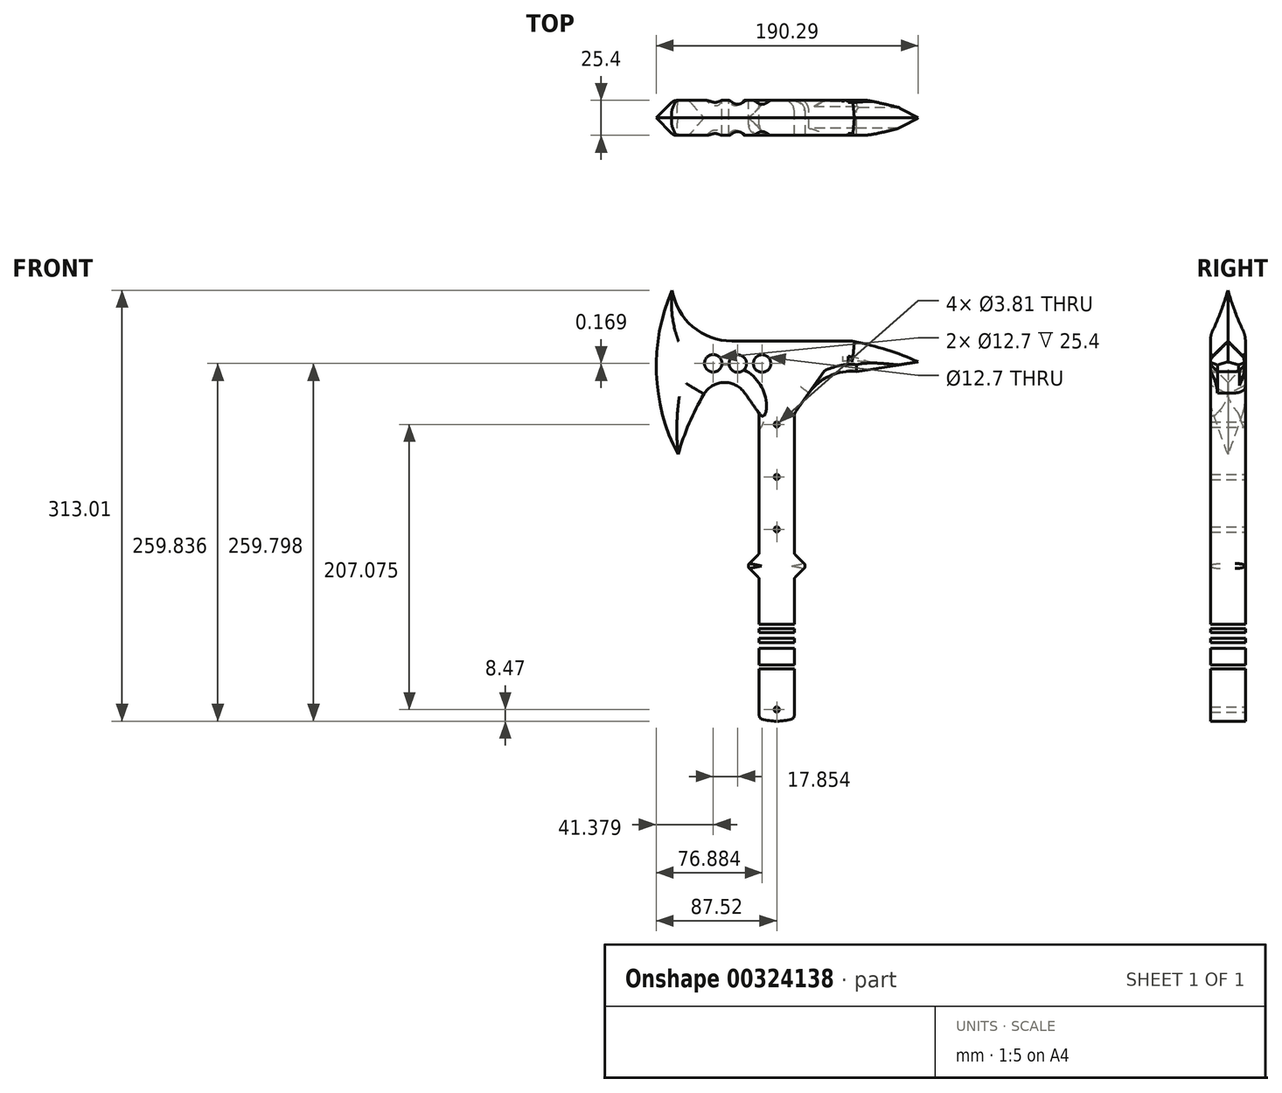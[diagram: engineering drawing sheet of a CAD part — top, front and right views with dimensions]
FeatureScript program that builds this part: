
annotation { "Feature Type Name" : "Feature", "Feature Type Description" : "" }
export const myFeature = defineFeature(function(context is Context, id is Id, definition is map)
    precondition{}
    {
        {
            var Q0;
            Q0=qCreatedBy(makeId("Front.planeOp"),FACE);
            var sketch = newSketch(context, id + "F0", { "sketchPlane" : qUnion([Q0])});
            skLineSegment(sketch, "E0", {"start": v(0, 35.02) * mm, "end": v(0, -35.92) * mm, "construction": true});
            skLineSegment(sketch, "E1", {"start": v(-43.38, 0) * mm, "end": v(43.38, 0) * mm, "construction": true});
            skLineSegment(sketch, "E2", {"start": v(-43.38, 44.66) * mm, "end": v(-43.38, -49.27) * mm, "construction": true});
            skLineSegment(sketch, "E3", {"start": v(43.38, 41.6) * mm, "end": v(43.38, -50.81) * mm, "construction": true});
            skLineSegment(sketch, "E4", {"start": v(58.14, -35.92) * mm, "end": v(-58.32, -35.92) * mm, "construction": true});
            skLineSegment(sketch, "E5", {"start": v(49.26, 35.02) * mm, "end": v(-56.77, 35.02) * mm, "construction": true});
            skArc(sketch, "E6", {"start": v(-10.89, -36.51) * mm, "mid": v(0, -38.1) * mm, "end": v(10.89, -36.51) * mm});
            skLineSegment(sketch, "E7", {"start": v(-12.7, -34.08) * mm, "end": v(-12.7, 64.63) * mm});
            skLineSegment(sketch, "E8", {"start": v(12.7, -34.08) * mm, "end": v(12.7, 64.63) * mm});
            skLineSegment(sketch, "E9", {"start": v(-13.44, 66.42) * mm, "end": v(-19.88, 72.86) * mm});
            skLineSegment(sketch, "E10", {"start": v(-19.88, 76.46) * mm, "end": v(-13.44, 82.9) * mm});
            skLineSegment(sketch, "E11", {"start": v(13.44, 66.42) * mm, "end": v(19.88, 72.86) * mm});
            skLineSegment(sketch, "E12", {"start": v(19.88, 76.46) * mm, "end": v(13.44, 82.9) * mm});
            skLineSegment(sketch, "E13", {"start": v(-12.7, 84.7) * mm, "end": v(-12.7, 183.24) * mm});
            skLineSegment(sketch, "E14", {"start": v(12.7, 84.7) * mm, "end": v(12.7, 183.24) * mm});
            skCircle(sketch, "E15", {"center": v(0, -29.63) * mm, "radius": 1.9 * mm});
            skLineSegment(sketch, "E16", {"start": v(-13.85, 186.88) * mm, "end": v(-23.3, 200.37) * mm});
            skLineSegment(sketch, "E17", {"start": v(13.85, 186.88) * mm, "end": v(23.3, 200.37) * mm});
            skArc(sketch, "E18", {"start": v(23.3, 200.37) * mm, "mid": v(0, 210.13) * mm, "end": v(-23.3, 200.37) * mm});
            skArc(sketch, "E19", {"start": v(57.98, 215.9) * mm, "mid": v(38.62, 212.64) * mm, "end": v(23.3, 200.37) * mm});
            skLineSegment(sketch, "E20", {"start": v(57.98, 215.9) * mm, "end": v(102.77, 222.96) * mm});
            skLineSegment(sketch, "E21", {"start": v(54.6, 176.96) * mm, "end": v(54.6, 259.28) * mm, "construction": true});
            skArc(sketch, "E22", {"start": v(102.77, 222.96) * mm, "mid": v(79.13, 231.9) * mm, "end": v(54.6, 238.02) * mm});
            skLineSegment(sketch, "E23", {"start": v(54.6, 238.02) * mm, "end": v(-32.59, 238.02) * mm});
            skArc(sketch, "E24", {"start": v(-75.92, 274.91) * mm, "mid": v(-61.04, 248.5) * mm, "end": v(-32.59, 238.02) * mm});
            skArc(sketch, "E25", {"start": v(-75.92, 274.91) * mm, "mid": v(-87.43, 214.8) * mm, "end": v(-71.62, 155.66) * mm});
            skArc(sketch, "E26", {"start": v(-23.3, 200.37) * mm, "mid": v(-38.34, 207.92) * mm, "end": v(-52.92, 199.5) * mm});
            skArc(sketch, "E27", {"start": v(-52.92, 199.5) * mm, "mid": v(-63.68, 178.18) * mm, "end": v(-71.62, 155.66) * mm});
            skLineSegment(sketch, "E28", {"start": v(-12.7, -25.44) * mm, "end": v(12.7, -25.44) * mm});
            skLineSegment(sketch, "E29", {"start": v(-12.7, -21.2) * mm, "end": v(12.7, -21.2) * mm});
            skLineSegment(sketch, "E30", {"start": v(-12.7, -17) * mm, "end": v(12.7, -17) * mm});
            skLineSegment(sketch, "E31", {"start": v(-12.7, -17) * mm, "end": v(-12.7, -12.4) * mm});
            skLineSegment(sketch, "E32", {"start": v(-12.7, -12.4) * mm, "end": v(12.7, -12.4) * mm});
            skLineSegment(sketch, "E33", {"start": v(12.7, -12.4) * mm, "end": v(12.7, -17) * mm});
            skLineSegment(sketch, "E34", {"start": v(-12.7, -21.2) * mm, "end": v(-12.7, -25.44) * mm});
            skLineSegment(sketch, "E35", {"start": v(12.7, -21.2) * mm, "end": v(12.7, -25.44) * mm});
            skLineSegment(sketch, "E36", {"start": v(-12.7, -8.39) * mm, "end": v(12.7, -8.39) * mm});
            skLineSegment(sketch, "E37", {"start": v(12.7, -8.39) * mm, "end": v(12.7, -4.18) * mm});
            skLineSegment(sketch, "E38", {"start": v(12.7, -4.18) * mm, "end": v(-12.7, -4.18) * mm});
            skLineSegment(sketch, "E39", {"start": v(-12.7, -4.18) * mm, "end": v(-12.7, -8.39) * mm});
            skLineSegment(sketch, "E40", {"start": v(-12.7, 0) * mm, "end": v(-12.7, 2.84) * mm});
            skLineSegment(sketch, "E41", {"start": v(-12.7, 2.84) * mm, "end": v(12.7, 2.84) * mm});
            skLineSegment(sketch, "E42", {"start": v(12.7, 2.84) * mm, "end": v(12.7, 0) * mm});
            skLineSegment(sketch, "E43", {"start": v(12.7, 0) * mm, "end": v(-12.7, 0) * mm});
            skLineSegment(sketch, "E44", {"start": v(-12.7, 14.88) * mm, "end": v(-12.7, 18.87) * mm});
            skLineSegment(sketch, "E45", {"start": v(-12.7, 18.87) * mm, "end": v(12.7, 18.87) * mm});
            skLineSegment(sketch, "E46", {"start": v(12.7, 18.87) * mm, "end": v(12.7, 14.88) * mm});
            skLineSegment(sketch, "E47", {"start": v(12.7, 14.88) * mm, "end": v(-12.7, 14.88) * mm});
            skLineSegment(sketch, "E48", {"start": v(-12.7, 22.28) * mm, "end": v(-12.7, 26.29) * mm});
            skLineSegment(sketch, "E49", {"start": v(-12.7, 26.29) * mm, "end": v(12.7, 26.29) * mm});
            skLineSegment(sketch, "E50", {"start": v(12.7, 26.29) * mm, "end": v(12.7, 22.22) * mm});
            skLineSegment(sketch, "E51", {"start": v(12.7, 22.22) * mm, "end": v(-12.7, 22.28) * mm});
            skLineSegment(sketch, "E52", {"start": v(-12.7, 29.04) * mm, "end": v(-12.7, 32.42) * mm});
            skLineSegment(sketch, "E53", {"start": v(-12.7, 32.42) * mm, "end": v(12.7, 32.42) * mm});
            skLineSegment(sketch, "E54", {"start": v(12.7, 32.42) * mm, "end": v(12.7, 29.04) * mm});
            skLineSegment(sketch, "E55", {"start": v(12.7, 29.04) * mm, "end": v(-12.7, 29.04) * mm});
            skLineSegment(sketch, "E56", {"start": v(-12.7, 35.9) * mm, "end": v(12.7, 35.9) * mm});
            skLineSegment(sketch, "E57", {"start": v(12.7, 35.9) * mm, "end": v(12.7, 39.28) * mm});
            skLineSegment(sketch, "E58", {"start": v(12.7, 39.28) * mm, "end": v(-12.7, 39.28) * mm});
            skLineSegment(sketch, "E59", {"start": v(-12.7, 39.28) * mm, "end": v(-12.7, 35.9) * mm});
            skCircle(sketch, "E60", {"center": v(0, 101.25) * mm, "radius": 1.9 * mm});
            skCircle(sketch, "E61", {"center": v(0, 139.35) * mm, "radius": 1.9 * mm});
            skCircle(sketch, "E62", {"center": v(0, 177.45) * mm, "radius": 1.9 * mm});
            skLineSegment(sketch, "E63.0", {"start": v(54.6, 221.8) * mm, "end": v(78.22, 225.52) * mm});
            skArc(sketch, "E63.1", {"start": v(78.22, 225.52) * mm, "mid": v(26.91, 235.06) * mm, "end": v(-25.16, 231.67) * mm});
            skLineSegment(sketch, "E63.2", {"start": v(-25.16, 231.67) * mm, "end": v(-32.59, 231.67) * mm});
            skArc(sketch, "E63.4", {"start": v(-58.36, 202.77) * mm, "mid": v(-66.1, 188.24) * mm, "end": v(-72.57, 173.1) * mm});
            skArc(sketch, "E63.5", {"start": v(-75.9, 256.46) * mm, "mid": v(-81.07, 214.5) * mm, "end": v(-72.57, 173.1) * mm});
            skArc(sketch, "E63.6", {"start": v(-75.9, 256.46) * mm, "mid": v(-57.54, 238.3) * mm, "end": v(-32.59, 231.67) * mm});
            skArc(sketch, "E64", {"start": v(54.6, 221.8) * mm, "mid": v(37, 213.93) * mm, "end": v(23.3, 200.37) * mm});
            skArc(sketch, "E65", {"start": v(-23.3, 200.37) * mm, "mid": v(-40.1, 212.15) * mm, "end": v(-58.36, 202.77) * mm});
            skLineSegment(sketch, "E66", {"start": v(0, 227.4) * mm, "end": v(0, 218.31) * mm});
            skLineSegment(sketch, "E67", {"start": v(-75.92, 274.91) * mm, "end": v(-75.9, 256.46) * mm});
            skLineSegment(sketch, "E68", {"start": v(-72.57, 173.1) * mm, "end": v(-71.62, 155.66) * mm});
            skLineSegment(sketch, "E69", {"start": v(78.22, 225.52) * mm, "end": v(102.77, 222.96) * mm});
            skCircle(sketch, "E70", {"center": v(-28.29, 221.7) * mm, "radius": 6.35 * mm});
            skCircle(sketch, "E71", {"center": v(-10.64, 221.74) * mm, "radius": 6.35 * mm});
            skCircle(sketch, "E72", {"center": v(-46.14, 221.87) * mm, "radius": 6.35 * mm});
            skPoint(sketch, "E73.visualSharp", {"position": v(21.68, 74.66) * mm});
            skArc(sketch, "E73.filletArc", {"start": v(19.88, 72.86) * mm, "mid": v(20.63, 74.66) * mm, "end": v(19.88, 76.46) * mm});
            skPoint(sketch, "E74.visualSharp", {"position": v(-21.68, 74.66) * mm});
            skArc(sketch, "E74.filletArc", {"start": v(-19.88, 76.46) * mm, "mid": v(-20.63, 74.66) * mm, "end": v(-19.88, 72.86) * mm});
            skPoint(sketch, "E75.visualSharp", {"position": v(-12.7, 65.68) * mm});
            skArc(sketch, "E75.filletArc", {"start": v(-12.7, 64.63) * mm, "mid": v(-12.9, 65.6) * mm, "end": v(-13.44, 66.42) * mm});
            skPoint(sketch, "E76.visualSharp", {"position": v(-12.7, 83.64) * mm});
            skArc(sketch, "E76.filletArc", {"start": v(-13.44, 82.9) * mm, "mid": v(-12.9, 83.72) * mm, "end": v(-12.7, 84.7) * mm});
            skPoint(sketch, "E77.visualSharp", {"position": v(12.7, 83.64) * mm});
            skArc(sketch, "E77.filletArc", {"start": v(12.7, 84.7) * mm, "mid": v(12.9, 83.72) * mm, "end": v(13.44, 82.9) * mm});
            skPoint(sketch, "E78.visualSharp", {"position": v(12.7, 65.68) * mm});
            skArc(sketch, "E78.filletArc", {"start": v(13.44, 66.42) * mm, "mid": v(12.9, 65.6) * mm, "end": v(12.7, 64.63) * mm});
            skPoint(sketch, "E79.visualSharp", {"position": v(-12.7, -35.92) * mm});
            skArc(sketch, "E79.filletArc", {"start": v(-12.7, -34.08) * mm, "mid": v(-12.2, -35.6) * mm, "end": v(-10.89, -36.51) * mm});
            skPoint(sketch, "E80.visualSharp", {"position": v(12.7, -35.92) * mm});
            skArc(sketch, "E80.filletArc", {"start": v(10.89, -36.51) * mm, "mid": v(12.2, -35.6) * mm, "end": v(12.7, -34.08) * mm});
            skLineSegment(sketch, "E81", {"start": v(0, -99) * mm, "end": v(0, 328.41) * mm, "construction": true});
            skPoint(sketch, "E82.visualSharp", {"position": v(12.7, 185.24) * mm});
            skArc(sketch, "E82.filletArc", {"start": v(13.85, 186.88) * mm, "mid": v(13, 185.15) * mm, "end": v(12.7, 183.24) * mm});
            skPoint(sketch, "E83.visualSharp", {"position": v(-12.7, 185.24) * mm});
            skArc(sketch, "E83.filletArc", {"start": v(-12.7, 183.24) * mm, "mid": v(-13, 185.15) * mm, "end": v(-13.85, 186.88) * mm});
            skLineSegment(sketch, "E84", {"start": v(-65.34, 221.87) * mm, "end": v(21.4, 221.74) * mm});
            skPoint(sketch, "E85.endSnap0", {"position": v(-81.07, 214.5) * mm});
            skSolve(sketch);
        }
        {
            var Q0;
            Q0=makeQuery(id+"F0.imprint","IMPRINT",FACE,{"disambiguationData":[TD([[makeQuery(id+"F0.imprint","IMPRINT",EDGE,{"derivedFrom":sQuery(id+"F0.wireOp",EDGE,"E9")}),-1.0]])]});
            var Q1;
            Q1=makeQuery(id+"F0.imprint","IMPRINT",FACE,{"disambiguationData":[TD([[makeQuery(id+"F0.imprint","IMPRINT",EDGE,{"derivedFrom":sQuery(id+"F0.wireOp",EDGE,"E6")}),1.0]])]});
            var Q2;
            {var subQ0=sQuery(id+"F0.wireOp",EDGE,"E29");Q2=makeQuery(id+"F0.imprint","IMPRINT",FACE,{"disambiguationData":[TD([[makeQuery(id+"F0.imprint","IMPRINT",EDGE,{"derivedFrom":subQ0}),1.0]])]});}
            var Q3;
            Q3=makeQuery(id+"F0.imprint","IMPRINT",FACE,{"disambiguationData":[TD([[makeQuery(id+"F0.imprint","IMPRINT",EDGE,{"derivedFrom":sQuery(id+"F0.wireOp",EDGE,"E28")}),1.0]])]});
            var Q4;
            Q4=makeQuery(id+"F0.imprint","IMPRINT",FACE,{"disambiguationData":[TD([[makeQuery(id+"F0.imprint","IMPRINT",EDGE,{"derivedFrom":sQuery(id+"F0.wireOp",EDGE,"E30")}),1.0]])]});
            var Q5;
            {var subQ0=sQuery(id+"F0.wireOp",EDGE,"E32");Q5=makeQuery(id+"F0.imprint","IMPRINT",FACE,{"disambiguationData":[TD([[makeQuery(id+"F0.imprint","IMPRINT",EDGE,{"derivedFrom":subQ0}),1.0]])]});}
            var Q6;
            Q6=makeQuery(id+"F0.imprint","IMPRINT",FACE,{"disambiguationData":[TD([[makeQuery(id+"F0.imprint","IMPRINT",EDGE,{"derivedFrom":sQuery(id+"F0.wireOp",EDGE,"E36")}),1.0]])]});
            var Q7;
            {var subQ0=sQuery(id+"F0.wireOp",EDGE,"E38");Q7=makeQuery(id+"F0.imprint","IMPRINT",FACE,{"disambiguationData":[TD([[makeQuery(id+"F0.imprint","IMPRINT",EDGE,{"derivedFrom":subQ0}),-1.0]])]});}
            var Q8;
            Q8=makeQuery(id+"F0.imprint","IMPRINT",FACE,{"disambiguationData":[TD([[makeQuery(id+"F0.imprint","IMPRINT",EDGE,{"derivedFrom":sQuery(id+"F0.wireOp",EDGE,"E40")}),-1.0]])]});
            var Q9;
            {var subQ0=sQuery(id+"F0.wireOp",EDGE,"E41");Q9=makeQuery(id+"F0.imprint","IMPRINT",FACE,{"disambiguationData":[TD([[makeQuery(id+"F0.imprint","IMPRINT",EDGE,{"derivedFrom":subQ0}),1.0]])]});}
            var Q10;
            Q10=makeQuery(id+"F0.imprint","IMPRINT",FACE,{"disambiguationData":[TD([[makeQuery(id+"F0.imprint","IMPRINT",EDGE,{"derivedFrom":sQuery(id+"F0.wireOp",EDGE,"E44")}),-1.0]])]});
            var Q11;
            {var subQ0=sQuery(id+"F0.wireOp",EDGE,"E45");Q11=makeQuery(id+"F0.imprint","IMPRINT",FACE,{"disambiguationData":[TD([[makeQuery(id+"F0.imprint","IMPRINT",EDGE,{"derivedFrom":subQ0}),1.0]])]});}
            var Q12;
            Q12=makeQuery(id+"F0.imprint","IMPRINT",FACE,{"disambiguationData":[TD([[makeQuery(id+"F0.imprint","IMPRINT",EDGE,{"derivedFrom":sQuery(id+"F0.wireOp",EDGE,"E48")}),-1.0]])]});
            var Q13;
            {var subQ0=sQuery(id+"F0.wireOp",EDGE,"E49");Q13=makeQuery(id+"F0.imprint","IMPRINT",FACE,{"disambiguationData":[TD([[makeQuery(id+"F0.imprint","IMPRINT",EDGE,{"derivedFrom":subQ0}),1.0]])]});}
            var Q14;
            Q14=makeQuery(id+"F0.imprint","IMPRINT",FACE,{"disambiguationData":[TD([[makeQuery(id+"F0.imprint","IMPRINT",EDGE,{"derivedFrom":sQuery(id+"F0.wireOp",EDGE,"E52")}),-1.0]])]});
            var Q15;
            {var subQ0=sQuery(id+"F0.wireOp",EDGE,"E53");Q15=makeQuery(id+"F0.imprint","IMPRINT",FACE,{"disambiguationData":[TD([[makeQuery(id+"F0.imprint","IMPRINT",EDGE,{"derivedFrom":subQ0}),1.0]])]});}
            var Q16;
            Q16=makeQuery(id+"F0.imprint","IMPRINT",FACE,{"disambiguationData":[TD([[makeQuery(id+"F0.imprint","IMPRINT",EDGE,{"derivedFrom":sQuery(id+"F0.wireOp",EDGE,"E56")}),1.0]])]});
            var Q17;
            Q17=makeQuery(id+"F0.imprint","IMPRINT",FACE,{"disambiguationData":[TD([[makeQuery(id+"F0.imprint","IMPRINT",EDGE,{"derivedFrom":sQuery(id+"F0.wireOp",EDGE,"E18")}),-1.0]])]});
            extrude(context, id + "F1", {"entities" : qUnion([Q0, Q1, Q2, Q3, Q4, Q5, Q6, Q7, Q8, Q9, Q10, Q11, Q12, Q13, Q14, Q15, Q16, Q17]), "depth" : 25.4 * mm, "symmetric" : true});
        }
        {
            var Q0;
            Q0=makeQuery(id+"F0.imprint","IMPRINT",FACE,{"disambiguationData":[TD([[makeQuery(id+"F0.imprint","IMPRINT",EDGE,{"derivedFrom":sQuery(id+"F0.wireOp",EDGE,"E25")}),1.0]])]});
            var Q1;
            Q1=makeQuery(id+"F0.imprint","IMPRINT",FACE,{"disambiguationData":[TD([[makeQuery(id+"F0.imprint","IMPRINT",EDGE,{"derivedFrom":sQuery(id+"F0.wireOp",EDGE,"E19")}),-1.0]])]});
            var Q2;
            Q2=makeQuery(id+"F0.imprint","IMPRINT",FACE,{"disambiguationData":[TD([[makeQuery(id+"F0.imprint","IMPRINT",EDGE,{"derivedFrom":sQuery(id+"F0.wireOp",EDGE,"E26")}),-1.0]])]});
            var Q3;
            Q3=makeQuery(id+"F0.imprint","IMPRINT",FACE,{"disambiguationData":[TD([[makeQuery(id+"F0.imprint","IMPRINT",EDGE,{"derivedFrom":sQuery(id+"F0.wireOp",EDGE,"E22")}),1.0]])]});
            extrude(context, id + "F2", {"entities" : qUnion([Q0, Q1, Q2, Q3]), "operationType" : NewBodyOperationType.ADD, "depth" : 25.4 * mm, "symmetric" : true});
        }
        {
            var Q0;
            Q0=makeQuery(id+"F2.opExtrude","CAP_EDGE",EDGE,{"disambiguationData":[OSD([sQuery(id+"F0.wireOp",EDGE,"E25")])],"isStart":false});
            var Q1;
            Q1=makeQuery(id+"F2.opExtrude","CAP_EDGE",EDGE,{"disambiguationData":[OSD([sQuery(id+"F0.wireOp",EDGE,"E25")])],"isStart":true});
            chamfer(context, id + "F3", {"entities" : qUnion([Q0, Q1]), "width" : 12.7 * mm, "tangentPropagation" : true});
        }
        {
            var Q0;
            Q0=makeQuery(id+"F2.opExtrude","CAP_EDGE",EDGE,{"disambiguationData":[OSD([sQuery(id+"F0.wireOp",EDGE,"E27")])],"isStart":false});
            var Q1;
            Q1=makeQuery(id+"F2.opExtrude","CAP_EDGE",EDGE,{"disambiguationData":[OSD([sQuery(id+"F0.wireOp",EDGE,"E27")])],"isStart":true});
            chamfer(context, id + "F4", {"entities" : qUnion([Q0, Q1]), "width" : 12.7 * mm, "tangentPropagation" : true});
        }
        {
            var Q0;
            Q0=makeQuery(id+"F2.opExtrude","CAP_EDGE",EDGE,{"disambiguationData":[OSD([sQuery(id+"F0.wireOp",EDGE,"E24")])],"isStart":false});
            var Q1;
            Q1=makeQuery(id+"F2.opExtrude","CAP_EDGE",EDGE,{"disambiguationData":[OSD([sQuery(id+"F0.wireOp",EDGE,"E24")])],"isStart":true});
            chamfer(context, id + "F5", {"entities" : qUnion([Q0, Q1]), "width" : 12.7 * mm, "tangentPropagation" : true});
        }
        {
            var Q0;
            Q0=makeQuery(id+"F2.opExtrude","CAP_EDGE",EDGE,{"disambiguationData":[OSD([sQuery(id+"F0.wireOp",EDGE,"E22")])],"isStart":false});
            var Q1;
            Q1=makeQuery(id+"F2.opExtrude","CAP_EDGE",EDGE,{"disambiguationData":[OSD([sQuery(id+"F0.wireOp",EDGE,"E22")])],"isStart":true});
            chamfer(context, id + "F6", {"entities" : qUnion([Q0, Q1]), "width" : 12.7 * mm, "tangentPropagation" : true});
        }
        {
            var Q0;
            Q0=makeQuery(id+"F2.opExtrude","CAP_EDGE",EDGE,{"disambiguationData":[OSD([sQuery(id+"F0.wireOp",EDGE,"E19")])],"isStart":false});
            var Q1;
            Q1=makeQuery(id+"F2.opExtrude","CAP_EDGE",EDGE,{"disambiguationData":[OSD([sQuery(id+"F0.wireOp",EDGE,"E19")])],"isStart":true});
            var Q2;
            Q2=makeQuery(id+"F2.opExtrude","CAP_EDGE",EDGE,{"disambiguationData":[OSD([sQuery(id+"F0.wireOp",EDGE,"E20")])],"isStart":false});
            var Q3;
            Q3=makeQuery(id+"F2.opExtrude","CAP_EDGE",EDGE,{"disambiguationData":[OSD([sQuery(id+"F0.wireOp",EDGE,"E20")])],"isStart":true});
            chamfer(context, id + "F7", {"entities" : qUnion([Q0, Q1, Q2, Q3]), "width" : 5.08 * mm, "tangentPropagation" : true});
        }
        {
            var Q0;
            Q0=makeQuery(id+"F1.opExtrude","CAP_EDGE",EDGE,{"disambiguationData":[OSD([sQuery(id+"F0.wireOp",EDGE,"E13")])],"isStart":false});
            var Q1;
            Q1=makeQuery(id+"F1.opExtrude","CAP_EDGE",EDGE,{"disambiguationData":[OSD([sQuery(id+"F0.wireOp",EDGE,"E14")])],"isStart":true});
            fillet(context, id + "F8", {"entities" : qUnion([Q0, Q1]), "radius" : 7.62 * mm, "tangentPropagation" : true, "allowEdgeOverflow" : false});
        }
        {
            var Q0;
            {var subQ0=sQuery(id+"F0.wireOp",EDGE,"E23");Q0=makeQuery(id+"F6.opChamfer","BLEND_EDGE",EDGE,{"blendedFrom":[makeQuery(id+"F2.opExtrude","CAP_EDGE",EDGE,{"disambiguationData":[OSD([sQuery(id+"F0.wireOp",EDGE,"E22")])],"isStart":false}),makeQuery(id+"F5.opChamfer","BLEND_FACE",FACE,{"disambiguationData":[OSD([subQ0]),TDD([makeQuery(id+"F2.opExtrude","CAP_EDGE",EDGE,{"disambiguationData":[OSD([subQ0])],"isStart":false})])]})],"blendedInto":[makeQuery(id+"F5.opChamfer","BLEND_FACE",FACE,{"disambiguationData":[OSD([subQ0]),TDD([makeQuery(id+"F2.opExtrude","CAP_EDGE",EDGE,{"disambiguationData":[OSD([subQ0])],"isStart":false})])]})]});}
            var Q1;
            {var subQ0=sQuery(id+"F0.wireOp",EDGE,"E23");Q1=makeQuery(id+"F6.opChamfer","BLEND_EDGE",EDGE,{"blendedFrom":[makeQuery(id+"F2.opExtrude","CAP_EDGE",EDGE,{"disambiguationData":[OSD([sQuery(id+"F0.wireOp",EDGE,"E22")])],"isStart":true}),makeQuery(id+"F5.opChamfer","BLEND_FACE",FACE,{"disambiguationData":[OSD([subQ0]),TDD([makeQuery(id+"F2.opExtrude","CAP_EDGE",EDGE,{"disambiguationData":[OSD([subQ0])],"isStart":true})])]})],"blendedInto":[makeQuery(id+"F5.opChamfer","BLEND_FACE",FACE,{"disambiguationData":[OSD([subQ0]),TDD([makeQuery(id+"F2.opExtrude","CAP_EDGE",EDGE,{"disambiguationData":[OSD([subQ0])],"isStart":true})])]})]});}
            fillet(context, id + "F9", {"entities" : qUnion([Q0, Q1]), "radius" : 25.4 * mm, "tangentPropagation" : true, "allowEdgeOverflow" : false});
        }
        {
            var Q0;
            {var subQ0=sQuery(id+"F0.wireOp",EDGE,"E65");var subQ1=sQuery(id+"F0.wireOp",EDGE,"E64");var subQ2=sQuery(id+"F0.wireOp",EDGE,"E63.6");var subQ3=sQuery(id+"F0.wireOp",EDGE,"E63.5");var subQ4=sQuery(id+"F0.wireOp",EDGE,"E63.4");var subQ5=sQuery(id+"F0.wireOp",EDGE,"E63.2");var subQ6=sQuery(id+"F0.wireOp",EDGE,"E63.1");var subQ7=sQuery(id+"F0.wireOp",EDGE,"E63.0");var subQ8=sQuery(id+"F0.wireOp",EDGE,"E24");Q0=makeQuery(id+"F5.opChamfer","BLEND_EDGE",EDGE,{"disambiguationData":[OD(1.0)],"blendedFrom":[makeQuery(id+"F2.opExtrude","CAP_EDGE",EDGE,{"disambiguationData":[OSD([subQ8])],"isStart":false}),makeQuery(id+"F2.boolean.opBoolean","MERGE",FACE,{"derivedFrom":[makeQuery(id+"F1.opExtrude","CAP_FACE",FACE,{"disambiguationData":[OSD([sQuery(id+"F0.wireOp",EDGE,"E6"),sQuery(id+"F0.wireOp",EDGE,"E7"),sQuery(id+"F0.wireOp",EDGE,"E8"),sQuery(id+"F0.wireOp",EDGE,"E9"),sQuery(id+"F0.wireOp",EDGE,"E10"),sQuery(id+"F0.wireOp",EDGE,"E11"),sQuery(id+"F0.wireOp",EDGE,"E12"),sQuery(id+"F0.wireOp",EDGE,"E13"),sQuery(id+"F0.wireOp",EDGE,"E14"),sQuery(id+"F0.wireOp",EDGE,"E15"),sQuery(id+"F0.wireOp",EDGE,"E16"),sQuery(id+"F0.wireOp",EDGE,"E17"),sQuery(id+"F0.wireOp",EDGE,"E31"),sQuery(id+"F0.wireOp",EDGE,"E33"),sQuery(id+"F0.wireOp",EDGE,"E34"),sQuery(id+"F0.wireOp",EDGE,"E35"),sQuery(id+"F0.wireOp",EDGE,"E37"),sQuery(id+"F0.wireOp",EDGE,"E39"),sQuery(id+"F0.wireOp",EDGE,"E40"),sQuery(id+"F0.wireOp",EDGE,"E42"),sQuery(id+"F0.wireOp",EDGE,"E44"),sQuery(id+"F0.wireOp",EDGE,"E46"),sQuery(id+"F0.wireOp",EDGE,"E48"),sQuery(id+"F0.wireOp",EDGE,"E50"),sQuery(id+"F0.wireOp",EDGE,"E52"),sQuery(id+"F0.wireOp",EDGE,"E54"),sQuery(id+"F0.wireOp",EDGE,"E57"),sQuery(id+"F0.wireOp",EDGE,"E59"),sQuery(id+"F0.wireOp",EDGE,"E60"),sQuery(id+"F0.wireOp",EDGE,"E61"),sQuery(id+"F0.wireOp",EDGE,"E62"),subQ7,subQ6,subQ5,subQ4,subQ3,subQ2,subQ1,subQ0,sQuery(id+"F0.wireOp",EDGE,"E70"),sQuery(id+"F0.wireOp",EDGE,"E71"),sQuery(id+"F0.wireOp",EDGE,"E72"),sQuery(id+"F0.wireOp",EDGE,"E73.filletArc"),sQuery(id+"F0.wireOp",EDGE,"E74.filletArc"),sQuery(id+"F0.wireOp",EDGE,"E75.filletArc"),sQuery(id+"F0.wireOp",EDGE,"E76.filletArc"),sQuery(id+"F0.wireOp",EDGE,"E77.filletArc"),sQuery(id+"F0.wireOp",EDGE,"E78.filletArc"),sQuery(id+"F0.wireOp",EDGE,"E79.filletArc"),sQuery(id+"F0.wireOp",EDGE,"E80.filletArc"),sQuery(id+"F0.wireOp",EDGE,"E82.filletArc"),sQuery(id+"F0.wireOp",EDGE,"E83.filletArc")])],"isStart":false}),makeQuery(id+"F2.opExtrude","CAP_FACE",FACE,{"disambiguationData":[OSD([sQuery(id+"F0.wireOp",EDGE,"E19"),sQuery(id+"F0.wireOp",EDGE,"E20"),sQuery(id+"F0.wireOp",EDGE,"E22"),sQuery(id+"F0.wireOp",EDGE,"E23"),subQ8,sQuery(id+"F0.wireOp",EDGE,"E25"),sQuery(id+"F0.wireOp",EDGE,"E26"),sQuery(id+"F0.wireOp",EDGE,"E27"),subQ7,subQ6,subQ5,subQ4,subQ3,subQ2,subQ1,subQ0])],"isStart":false})]})],"blendedInto":[makeQuery(id+"F2.boolean.opBoolean","MERGE",FACE,{"derivedFrom":[makeQuery(id+"F1.opExtrude","CAP_FACE",FACE,{"disambiguationData":[OSD([sQuery(id+"F0.wireOp",EDGE,"E6"),sQuery(id+"F0.wireOp",EDGE,"E7"),sQuery(id+"F0.wireOp",EDGE,"E8"),sQuery(id+"F0.wireOp",EDGE,"E9"),sQuery(id+"F0.wireOp",EDGE,"E10"),sQuery(id+"F0.wireOp",EDGE,"E11"),sQuery(id+"F0.wireOp",EDGE,"E12"),sQuery(id+"F0.wireOp",EDGE,"E13"),sQuery(id+"F0.wireOp",EDGE,"E14"),sQuery(id+"F0.wireOp",EDGE,"E15"),sQuery(id+"F0.wireOp",EDGE,"E16"),sQuery(id+"F0.wireOp",EDGE,"E17"),sQuery(id+"F0.wireOp",EDGE,"E31"),sQuery(id+"F0.wireOp",EDGE,"E33"),sQuery(id+"F0.wireOp",EDGE,"E34"),sQuery(id+"F0.wireOp",EDGE,"E35"),sQuery(id+"F0.wireOp",EDGE,"E37"),sQuery(id+"F0.wireOp",EDGE,"E39"),sQuery(id+"F0.wireOp",EDGE,"E40"),sQuery(id+"F0.wireOp",EDGE,"E42"),sQuery(id+"F0.wireOp",EDGE,"E44"),sQuery(id+"F0.wireOp",EDGE,"E46"),sQuery(id+"F0.wireOp",EDGE,"E48"),sQuery(id+"F0.wireOp",EDGE,"E50"),sQuery(id+"F0.wireOp",EDGE,"E52"),sQuery(id+"F0.wireOp",EDGE,"E54"),sQuery(id+"F0.wireOp",EDGE,"E57"),sQuery(id+"F0.wireOp",EDGE,"E59"),sQuery(id+"F0.wireOp",EDGE,"E60"),sQuery(id+"F0.wireOp",EDGE,"E61"),sQuery(id+"F0.wireOp",EDGE,"E62"),subQ7,subQ6,subQ5,subQ4,subQ3,subQ2,subQ1,subQ0,sQuery(id+"F0.wireOp",EDGE,"E70"),sQuery(id+"F0.wireOp",EDGE,"E71"),sQuery(id+"F0.wireOp",EDGE,"E72"),sQuery(id+"F0.wireOp",EDGE,"E73.filletArc"),sQuery(id+"F0.wireOp",EDGE,"E74.filletArc"),sQuery(id+"F0.wireOp",EDGE,"E75.filletArc"),sQuery(id+"F0.wireOp",EDGE,"E76.filletArc"),sQuery(id+"F0.wireOp",EDGE,"E77.filletArc"),sQuery(id+"F0.wireOp",EDGE,"E78.filletArc"),sQuery(id+"F0.wireOp",EDGE,"E79.filletArc"),sQuery(id+"F0.wireOp",EDGE,"E80.filletArc"),sQuery(id+"F0.wireOp",EDGE,"E82.filletArc"),sQuery(id+"F0.wireOp",EDGE,"E83.filletArc")])],"isStart":false}),makeQuery(id+"F2.opExtrude","CAP_FACE",FACE,{"disambiguationData":[OSD([sQuery(id+"F0.wireOp",EDGE,"E19"),sQuery(id+"F0.wireOp",EDGE,"E20"),sQuery(id+"F0.wireOp",EDGE,"E22"),sQuery(id+"F0.wireOp",EDGE,"E23"),subQ8,sQuery(id+"F0.wireOp",EDGE,"E25"),sQuery(id+"F0.wireOp",EDGE,"E26"),sQuery(id+"F0.wireOp",EDGE,"E27"),subQ7,subQ6,subQ5,subQ4,subQ3,subQ2,subQ1,subQ0])],"isStart":false})]})]});}
            var Q1;
            {var subQ0=sQuery(id+"F0.wireOp",EDGE,"E65");var subQ1=sQuery(id+"F0.wireOp",EDGE,"E64");var subQ2=sQuery(id+"F0.wireOp",EDGE,"E63.6");var subQ3=sQuery(id+"F0.wireOp",EDGE,"E63.5");var subQ4=sQuery(id+"F0.wireOp",EDGE,"E63.4");var subQ5=sQuery(id+"F0.wireOp",EDGE,"E63.2");var subQ6=sQuery(id+"F0.wireOp",EDGE,"E63.1");var subQ7=sQuery(id+"F0.wireOp",EDGE,"E63.0");var subQ8=sQuery(id+"F0.wireOp",EDGE,"E25");Q1=makeQuery(id+"F3.opChamfer","BLEND_EDGE",EDGE,{"blendedFrom":[makeQuery(id+"F2.opExtrude","CAP_EDGE",EDGE,{"disambiguationData":[OSD([subQ8])],"isStart":false}),makeQuery(id+"F2.boolean.opBoolean","MERGE",FACE,{"derivedFrom":[makeQuery(id+"F1.opExtrude","CAP_FACE",FACE,{"disambiguationData":[OSD([sQuery(id+"F0.wireOp",EDGE,"E6"),sQuery(id+"F0.wireOp",EDGE,"E7"),sQuery(id+"F0.wireOp",EDGE,"E8"),sQuery(id+"F0.wireOp",EDGE,"E9"),sQuery(id+"F0.wireOp",EDGE,"E10"),sQuery(id+"F0.wireOp",EDGE,"E11"),sQuery(id+"F0.wireOp",EDGE,"E12"),sQuery(id+"F0.wireOp",EDGE,"E13"),sQuery(id+"F0.wireOp",EDGE,"E14"),sQuery(id+"F0.wireOp",EDGE,"E15"),sQuery(id+"F0.wireOp",EDGE,"E16"),sQuery(id+"F0.wireOp",EDGE,"E17"),sQuery(id+"F0.wireOp",EDGE,"E31"),sQuery(id+"F0.wireOp",EDGE,"E33"),sQuery(id+"F0.wireOp",EDGE,"E34"),sQuery(id+"F0.wireOp",EDGE,"E35"),sQuery(id+"F0.wireOp",EDGE,"E37"),sQuery(id+"F0.wireOp",EDGE,"E39"),sQuery(id+"F0.wireOp",EDGE,"E40"),sQuery(id+"F0.wireOp",EDGE,"E42"),sQuery(id+"F0.wireOp",EDGE,"E44"),sQuery(id+"F0.wireOp",EDGE,"E46"),sQuery(id+"F0.wireOp",EDGE,"E48"),sQuery(id+"F0.wireOp",EDGE,"E50"),sQuery(id+"F0.wireOp",EDGE,"E52"),sQuery(id+"F0.wireOp",EDGE,"E54"),sQuery(id+"F0.wireOp",EDGE,"E57"),sQuery(id+"F0.wireOp",EDGE,"E59"),sQuery(id+"F0.wireOp",EDGE,"E60"),sQuery(id+"F0.wireOp",EDGE,"E61"),sQuery(id+"F0.wireOp",EDGE,"E62"),subQ7,subQ6,subQ5,subQ4,subQ3,subQ2,subQ1,subQ0,sQuery(id+"F0.wireOp",EDGE,"E70"),sQuery(id+"F0.wireOp",EDGE,"E71"),sQuery(id+"F0.wireOp",EDGE,"E72"),sQuery(id+"F0.wireOp",EDGE,"E73.filletArc"),sQuery(id+"F0.wireOp",EDGE,"E74.filletArc"),sQuery(id+"F0.wireOp",EDGE,"E75.filletArc"),sQuery(id+"F0.wireOp",EDGE,"E76.filletArc"),sQuery(id+"F0.wireOp",EDGE,"E77.filletArc"),sQuery(id+"F0.wireOp",EDGE,"E78.filletArc"),sQuery(id+"F0.wireOp",EDGE,"E79.filletArc"),sQuery(id+"F0.wireOp",EDGE,"E80.filletArc"),sQuery(id+"F0.wireOp",EDGE,"E82.filletArc"),sQuery(id+"F0.wireOp",EDGE,"E83.filletArc")])],"isStart":false}),makeQuery(id+"F2.opExtrude","CAP_FACE",FACE,{"disambiguationData":[OSD([sQuery(id+"F0.wireOp",EDGE,"E19"),sQuery(id+"F0.wireOp",EDGE,"E20"),sQuery(id+"F0.wireOp",EDGE,"E22"),sQuery(id+"F0.wireOp",EDGE,"E23"),sQuery(id+"F0.wireOp",EDGE,"E24"),subQ8,sQuery(id+"F0.wireOp",EDGE,"E26"),sQuery(id+"F0.wireOp",EDGE,"E27"),subQ7,subQ6,subQ5,subQ4,subQ3,subQ2,subQ1,subQ0])],"isStart":false})]})],"blendedInto":[makeQuery(id+"F2.boolean.opBoolean","MERGE",FACE,{"derivedFrom":[makeQuery(id+"F1.opExtrude","CAP_FACE",FACE,{"disambiguationData":[OSD([sQuery(id+"F0.wireOp",EDGE,"E6"),sQuery(id+"F0.wireOp",EDGE,"E7"),sQuery(id+"F0.wireOp",EDGE,"E8"),sQuery(id+"F0.wireOp",EDGE,"E9"),sQuery(id+"F0.wireOp",EDGE,"E10"),sQuery(id+"F0.wireOp",EDGE,"E11"),sQuery(id+"F0.wireOp",EDGE,"E12"),sQuery(id+"F0.wireOp",EDGE,"E13"),sQuery(id+"F0.wireOp",EDGE,"E14"),sQuery(id+"F0.wireOp",EDGE,"E15"),sQuery(id+"F0.wireOp",EDGE,"E16"),sQuery(id+"F0.wireOp",EDGE,"E17"),sQuery(id+"F0.wireOp",EDGE,"E31"),sQuery(id+"F0.wireOp",EDGE,"E33"),sQuery(id+"F0.wireOp",EDGE,"E34"),sQuery(id+"F0.wireOp",EDGE,"E35"),sQuery(id+"F0.wireOp",EDGE,"E37"),sQuery(id+"F0.wireOp",EDGE,"E39"),sQuery(id+"F0.wireOp",EDGE,"E40"),sQuery(id+"F0.wireOp",EDGE,"E42"),sQuery(id+"F0.wireOp",EDGE,"E44"),sQuery(id+"F0.wireOp",EDGE,"E46"),sQuery(id+"F0.wireOp",EDGE,"E48"),sQuery(id+"F0.wireOp",EDGE,"E50"),sQuery(id+"F0.wireOp",EDGE,"E52"),sQuery(id+"F0.wireOp",EDGE,"E54"),sQuery(id+"F0.wireOp",EDGE,"E57"),sQuery(id+"F0.wireOp",EDGE,"E59"),sQuery(id+"F0.wireOp",EDGE,"E60"),sQuery(id+"F0.wireOp",EDGE,"E61"),sQuery(id+"F0.wireOp",EDGE,"E62"),subQ7,subQ6,subQ5,subQ4,subQ3,subQ2,subQ1,subQ0,sQuery(id+"F0.wireOp",EDGE,"E70"),sQuery(id+"F0.wireOp",EDGE,"E71"),sQuery(id+"F0.wireOp",EDGE,"E72"),sQuery(id+"F0.wireOp",EDGE,"E73.filletArc"),sQuery(id+"F0.wireOp",EDGE,"E74.filletArc"),sQuery(id+"F0.wireOp",EDGE,"E75.filletArc"),sQuery(id+"F0.wireOp",EDGE,"E76.filletArc"),sQuery(id+"F0.wireOp",EDGE,"E77.filletArc"),sQuery(id+"F0.wireOp",EDGE,"E78.filletArc"),sQuery(id+"F0.wireOp",EDGE,"E79.filletArc"),sQuery(id+"F0.wireOp",EDGE,"E80.filletArc"),sQuery(id+"F0.wireOp",EDGE,"E82.filletArc"),sQuery(id+"F0.wireOp",EDGE,"E83.filletArc")])],"isStart":false}),makeQuery(id+"F2.opExtrude","CAP_FACE",FACE,{"disambiguationData":[OSD([sQuery(id+"F0.wireOp",EDGE,"E19"),sQuery(id+"F0.wireOp",EDGE,"E20"),sQuery(id+"F0.wireOp",EDGE,"E22"),sQuery(id+"F0.wireOp",EDGE,"E23"),sQuery(id+"F0.wireOp",EDGE,"E24"),subQ8,sQuery(id+"F0.wireOp",EDGE,"E26"),sQuery(id+"F0.wireOp",EDGE,"E27"),subQ7,subQ6,subQ5,subQ4,subQ3,subQ2,subQ1,subQ0])],"isStart":false})]})]});}
            var Q2;
            {var subQ0=sQuery(id+"F0.wireOp",EDGE,"E65");var subQ1=sQuery(id+"F0.wireOp",EDGE,"E64");var subQ2=sQuery(id+"F0.wireOp",EDGE,"E63.6");var subQ3=sQuery(id+"F0.wireOp",EDGE,"E63.5");var subQ4=sQuery(id+"F0.wireOp",EDGE,"E63.4");var subQ5=sQuery(id+"F0.wireOp",EDGE,"E63.2");var subQ6=sQuery(id+"F0.wireOp",EDGE,"E63.1");var subQ7=sQuery(id+"F0.wireOp",EDGE,"E63.0");var subQ8=sQuery(id+"F0.wireOp",EDGE,"E26");Q2=makeQuery(id+"F4.opChamfer","BLEND_EDGE",EDGE,{"disambiguationData":[OD(1.0)],"blendedFrom":[makeQuery(id+"F2.opExtrude","CAP_EDGE",EDGE,{"disambiguationData":[OSD([subQ8])],"isStart":false}),makeQuery(id+"F2.boolean.opBoolean","MERGE",FACE,{"derivedFrom":[makeQuery(id+"F1.opExtrude","CAP_FACE",FACE,{"disambiguationData":[OSD([sQuery(id+"F0.wireOp",EDGE,"E6"),sQuery(id+"F0.wireOp",EDGE,"E7"),sQuery(id+"F0.wireOp",EDGE,"E8"),sQuery(id+"F0.wireOp",EDGE,"E9"),sQuery(id+"F0.wireOp",EDGE,"E10"),sQuery(id+"F0.wireOp",EDGE,"E11"),sQuery(id+"F0.wireOp",EDGE,"E12"),sQuery(id+"F0.wireOp",EDGE,"E13"),sQuery(id+"F0.wireOp",EDGE,"E14"),sQuery(id+"F0.wireOp",EDGE,"E15"),sQuery(id+"F0.wireOp",EDGE,"E16"),sQuery(id+"F0.wireOp",EDGE,"E17"),sQuery(id+"F0.wireOp",EDGE,"E31"),sQuery(id+"F0.wireOp",EDGE,"E33"),sQuery(id+"F0.wireOp",EDGE,"E34"),sQuery(id+"F0.wireOp",EDGE,"E35"),sQuery(id+"F0.wireOp",EDGE,"E37"),sQuery(id+"F0.wireOp",EDGE,"E39"),sQuery(id+"F0.wireOp",EDGE,"E40"),sQuery(id+"F0.wireOp",EDGE,"E42"),sQuery(id+"F0.wireOp",EDGE,"E44"),sQuery(id+"F0.wireOp",EDGE,"E46"),sQuery(id+"F0.wireOp",EDGE,"E48"),sQuery(id+"F0.wireOp",EDGE,"E50"),sQuery(id+"F0.wireOp",EDGE,"E52"),sQuery(id+"F0.wireOp",EDGE,"E54"),sQuery(id+"F0.wireOp",EDGE,"E57"),sQuery(id+"F0.wireOp",EDGE,"E59"),sQuery(id+"F0.wireOp",EDGE,"E60"),sQuery(id+"F0.wireOp",EDGE,"E61"),sQuery(id+"F0.wireOp",EDGE,"E62"),subQ7,subQ6,subQ5,subQ4,subQ3,subQ2,subQ1,subQ0,sQuery(id+"F0.wireOp",EDGE,"E70"),sQuery(id+"F0.wireOp",EDGE,"E71"),sQuery(id+"F0.wireOp",EDGE,"E72"),sQuery(id+"F0.wireOp",EDGE,"E73.filletArc"),sQuery(id+"F0.wireOp",EDGE,"E74.filletArc"),sQuery(id+"F0.wireOp",EDGE,"E75.filletArc"),sQuery(id+"F0.wireOp",EDGE,"E76.filletArc"),sQuery(id+"F0.wireOp",EDGE,"E77.filletArc"),sQuery(id+"F0.wireOp",EDGE,"E78.filletArc"),sQuery(id+"F0.wireOp",EDGE,"E79.filletArc"),sQuery(id+"F0.wireOp",EDGE,"E80.filletArc"),sQuery(id+"F0.wireOp",EDGE,"E82.filletArc"),sQuery(id+"F0.wireOp",EDGE,"E83.filletArc")])],"isStart":false}),makeQuery(id+"F2.opExtrude","CAP_FACE",FACE,{"disambiguationData":[OSD([sQuery(id+"F0.wireOp",EDGE,"E19"),sQuery(id+"F0.wireOp",EDGE,"E20"),sQuery(id+"F0.wireOp",EDGE,"E22"),sQuery(id+"F0.wireOp",EDGE,"E23"),sQuery(id+"F0.wireOp",EDGE,"E24"),sQuery(id+"F0.wireOp",EDGE,"E25"),subQ8,sQuery(id+"F0.wireOp",EDGE,"E27"),subQ7,subQ6,subQ5,subQ4,subQ3,subQ2,subQ1,subQ0])],"isStart":false})]})],"blendedInto":[makeQuery(id+"F2.boolean.opBoolean","MERGE",FACE,{"derivedFrom":[makeQuery(id+"F1.opExtrude","CAP_FACE",FACE,{"disambiguationData":[OSD([sQuery(id+"F0.wireOp",EDGE,"E6"),sQuery(id+"F0.wireOp",EDGE,"E7"),sQuery(id+"F0.wireOp",EDGE,"E8"),sQuery(id+"F0.wireOp",EDGE,"E9"),sQuery(id+"F0.wireOp",EDGE,"E10"),sQuery(id+"F0.wireOp",EDGE,"E11"),sQuery(id+"F0.wireOp",EDGE,"E12"),sQuery(id+"F0.wireOp",EDGE,"E13"),sQuery(id+"F0.wireOp",EDGE,"E14"),sQuery(id+"F0.wireOp",EDGE,"E15"),sQuery(id+"F0.wireOp",EDGE,"E16"),sQuery(id+"F0.wireOp",EDGE,"E17"),sQuery(id+"F0.wireOp",EDGE,"E31"),sQuery(id+"F0.wireOp",EDGE,"E33"),sQuery(id+"F0.wireOp",EDGE,"E34"),sQuery(id+"F0.wireOp",EDGE,"E35"),sQuery(id+"F0.wireOp",EDGE,"E37"),sQuery(id+"F0.wireOp",EDGE,"E39"),sQuery(id+"F0.wireOp",EDGE,"E40"),sQuery(id+"F0.wireOp",EDGE,"E42"),sQuery(id+"F0.wireOp",EDGE,"E44"),sQuery(id+"F0.wireOp",EDGE,"E46"),sQuery(id+"F0.wireOp",EDGE,"E48"),sQuery(id+"F0.wireOp",EDGE,"E50"),sQuery(id+"F0.wireOp",EDGE,"E52"),sQuery(id+"F0.wireOp",EDGE,"E54"),sQuery(id+"F0.wireOp",EDGE,"E57"),sQuery(id+"F0.wireOp",EDGE,"E59"),sQuery(id+"F0.wireOp",EDGE,"E60"),sQuery(id+"F0.wireOp",EDGE,"E61"),sQuery(id+"F0.wireOp",EDGE,"E62"),subQ7,subQ6,subQ5,subQ4,subQ3,subQ2,subQ1,subQ0,sQuery(id+"F0.wireOp",EDGE,"E70"),sQuery(id+"F0.wireOp",EDGE,"E71"),sQuery(id+"F0.wireOp",EDGE,"E72"),sQuery(id+"F0.wireOp",EDGE,"E73.filletArc"),sQuery(id+"F0.wireOp",EDGE,"E74.filletArc"),sQuery(id+"F0.wireOp",EDGE,"E75.filletArc"),sQuery(id+"F0.wireOp",EDGE,"E76.filletArc"),sQuery(id+"F0.wireOp",EDGE,"E77.filletArc"),sQuery(id+"F0.wireOp",EDGE,"E78.filletArc"),sQuery(id+"F0.wireOp",EDGE,"E79.filletArc"),sQuery(id+"F0.wireOp",EDGE,"E80.filletArc"),sQuery(id+"F0.wireOp",EDGE,"E82.filletArc"),sQuery(id+"F0.wireOp",EDGE,"E83.filletArc")])],"isStart":false}),makeQuery(id+"F2.opExtrude","CAP_FACE",FACE,{"disambiguationData":[OSD([sQuery(id+"F0.wireOp",EDGE,"E19"),sQuery(id+"F0.wireOp",EDGE,"E20"),sQuery(id+"F0.wireOp",EDGE,"E22"),sQuery(id+"F0.wireOp",EDGE,"E23"),sQuery(id+"F0.wireOp",EDGE,"E24"),sQuery(id+"F0.wireOp",EDGE,"E25"),subQ8,sQuery(id+"F0.wireOp",EDGE,"E27"),subQ7,subQ6,subQ5,subQ4,subQ3,subQ2,subQ1,subQ0])],"isStart":false})]})]});}
            var Q3;
            {var subQ0=sQuery(id+"F0.wireOp",EDGE,"E65");var subQ1=sQuery(id+"F0.wireOp",EDGE,"E64");var subQ2=sQuery(id+"F0.wireOp",EDGE,"E63.6");var subQ3=sQuery(id+"F0.wireOp",EDGE,"E63.5");var subQ4=sQuery(id+"F0.wireOp",EDGE,"E63.4");var subQ5=sQuery(id+"F0.wireOp",EDGE,"E63.2");var subQ6=sQuery(id+"F0.wireOp",EDGE,"E63.1");var subQ7=sQuery(id+"F0.wireOp",EDGE,"E63.0");var subQ8=sQuery(id+"F0.wireOp",EDGE,"E26");Q3=makeQuery(id+"F4.opChamfer","BLEND_EDGE",EDGE,{"disambiguationData":[OD(2.0)],"blendedFrom":[makeQuery(id+"F2.opExtrude","CAP_EDGE",EDGE,{"disambiguationData":[OSD([subQ8])],"isStart":false}),makeQuery(id+"F2.boolean.opBoolean","MERGE",FACE,{"derivedFrom":[makeQuery(id+"F1.opExtrude","CAP_FACE",FACE,{"disambiguationData":[OSD([sQuery(id+"F0.wireOp",EDGE,"E6"),sQuery(id+"F0.wireOp",EDGE,"E7"),sQuery(id+"F0.wireOp",EDGE,"E8"),sQuery(id+"F0.wireOp",EDGE,"E9"),sQuery(id+"F0.wireOp",EDGE,"E10"),sQuery(id+"F0.wireOp",EDGE,"E11"),sQuery(id+"F0.wireOp",EDGE,"E12"),sQuery(id+"F0.wireOp",EDGE,"E13"),sQuery(id+"F0.wireOp",EDGE,"E14"),sQuery(id+"F0.wireOp",EDGE,"E15"),sQuery(id+"F0.wireOp",EDGE,"E16"),sQuery(id+"F0.wireOp",EDGE,"E17"),sQuery(id+"F0.wireOp",EDGE,"E31"),sQuery(id+"F0.wireOp",EDGE,"E33"),sQuery(id+"F0.wireOp",EDGE,"E34"),sQuery(id+"F0.wireOp",EDGE,"E35"),sQuery(id+"F0.wireOp",EDGE,"E37"),sQuery(id+"F0.wireOp",EDGE,"E39"),sQuery(id+"F0.wireOp",EDGE,"E40"),sQuery(id+"F0.wireOp",EDGE,"E42"),sQuery(id+"F0.wireOp",EDGE,"E44"),sQuery(id+"F0.wireOp",EDGE,"E46"),sQuery(id+"F0.wireOp",EDGE,"E48"),sQuery(id+"F0.wireOp",EDGE,"E50"),sQuery(id+"F0.wireOp",EDGE,"E52"),sQuery(id+"F0.wireOp",EDGE,"E54"),sQuery(id+"F0.wireOp",EDGE,"E57"),sQuery(id+"F0.wireOp",EDGE,"E59"),sQuery(id+"F0.wireOp",EDGE,"E60"),sQuery(id+"F0.wireOp",EDGE,"E61"),sQuery(id+"F0.wireOp",EDGE,"E62"),subQ7,subQ6,subQ5,subQ4,subQ3,subQ2,subQ1,subQ0,sQuery(id+"F0.wireOp",EDGE,"E70"),sQuery(id+"F0.wireOp",EDGE,"E71"),sQuery(id+"F0.wireOp",EDGE,"E72"),sQuery(id+"F0.wireOp",EDGE,"E73.filletArc"),sQuery(id+"F0.wireOp",EDGE,"E74.filletArc"),sQuery(id+"F0.wireOp",EDGE,"E75.filletArc"),sQuery(id+"F0.wireOp",EDGE,"E76.filletArc"),sQuery(id+"F0.wireOp",EDGE,"E77.filletArc"),sQuery(id+"F0.wireOp",EDGE,"E78.filletArc"),sQuery(id+"F0.wireOp",EDGE,"E79.filletArc"),sQuery(id+"F0.wireOp",EDGE,"E80.filletArc"),sQuery(id+"F0.wireOp",EDGE,"E82.filletArc"),sQuery(id+"F0.wireOp",EDGE,"E83.filletArc")])],"isStart":false}),makeQuery(id+"F2.opExtrude","CAP_FACE",FACE,{"disambiguationData":[OSD([sQuery(id+"F0.wireOp",EDGE,"E19"),sQuery(id+"F0.wireOp",EDGE,"E20"),sQuery(id+"F0.wireOp",EDGE,"E22"),sQuery(id+"F0.wireOp",EDGE,"E23"),sQuery(id+"F0.wireOp",EDGE,"E24"),sQuery(id+"F0.wireOp",EDGE,"E25"),subQ8,sQuery(id+"F0.wireOp",EDGE,"E27"),subQ7,subQ6,subQ5,subQ4,subQ3,subQ2,subQ1,subQ0])],"isStart":false})]})],"blendedInto":[makeQuery(id+"F2.boolean.opBoolean","MERGE",FACE,{"derivedFrom":[makeQuery(id+"F1.opExtrude","CAP_FACE",FACE,{"disambiguationData":[OSD([sQuery(id+"F0.wireOp",EDGE,"E6"),sQuery(id+"F0.wireOp",EDGE,"E7"),sQuery(id+"F0.wireOp",EDGE,"E8"),sQuery(id+"F0.wireOp",EDGE,"E9"),sQuery(id+"F0.wireOp",EDGE,"E10"),sQuery(id+"F0.wireOp",EDGE,"E11"),sQuery(id+"F0.wireOp",EDGE,"E12"),sQuery(id+"F0.wireOp",EDGE,"E13"),sQuery(id+"F0.wireOp",EDGE,"E14"),sQuery(id+"F0.wireOp",EDGE,"E15"),sQuery(id+"F0.wireOp",EDGE,"E16"),sQuery(id+"F0.wireOp",EDGE,"E17"),sQuery(id+"F0.wireOp",EDGE,"E31"),sQuery(id+"F0.wireOp",EDGE,"E33"),sQuery(id+"F0.wireOp",EDGE,"E34"),sQuery(id+"F0.wireOp",EDGE,"E35"),sQuery(id+"F0.wireOp",EDGE,"E37"),sQuery(id+"F0.wireOp",EDGE,"E39"),sQuery(id+"F0.wireOp",EDGE,"E40"),sQuery(id+"F0.wireOp",EDGE,"E42"),sQuery(id+"F0.wireOp",EDGE,"E44"),sQuery(id+"F0.wireOp",EDGE,"E46"),sQuery(id+"F0.wireOp",EDGE,"E48"),sQuery(id+"F0.wireOp",EDGE,"E50"),sQuery(id+"F0.wireOp",EDGE,"E52"),sQuery(id+"F0.wireOp",EDGE,"E54"),sQuery(id+"F0.wireOp",EDGE,"E57"),sQuery(id+"F0.wireOp",EDGE,"E59"),sQuery(id+"F0.wireOp",EDGE,"E60"),sQuery(id+"F0.wireOp",EDGE,"E61"),sQuery(id+"F0.wireOp",EDGE,"E62"),subQ7,subQ6,subQ5,subQ4,subQ3,subQ2,subQ1,subQ0,sQuery(id+"F0.wireOp",EDGE,"E70"),sQuery(id+"F0.wireOp",EDGE,"E71"),sQuery(id+"F0.wireOp",EDGE,"E72"),sQuery(id+"F0.wireOp",EDGE,"E73.filletArc"),sQuery(id+"F0.wireOp",EDGE,"E74.filletArc"),sQuery(id+"F0.wireOp",EDGE,"E75.filletArc"),sQuery(id+"F0.wireOp",EDGE,"E76.filletArc"),sQuery(id+"F0.wireOp",EDGE,"E77.filletArc"),sQuery(id+"F0.wireOp",EDGE,"E78.filletArc"),sQuery(id+"F0.wireOp",EDGE,"E79.filletArc"),sQuery(id+"F0.wireOp",EDGE,"E80.filletArc"),sQuery(id+"F0.wireOp",EDGE,"E82.filletArc"),sQuery(id+"F0.wireOp",EDGE,"E83.filletArc")])],"isStart":false}),makeQuery(id+"F2.opExtrude","CAP_FACE",FACE,{"disambiguationData":[OSD([sQuery(id+"F0.wireOp",EDGE,"E19"),sQuery(id+"F0.wireOp",EDGE,"E20"),sQuery(id+"F0.wireOp",EDGE,"E22"),sQuery(id+"F0.wireOp",EDGE,"E23"),sQuery(id+"F0.wireOp",EDGE,"E24"),sQuery(id+"F0.wireOp",EDGE,"E25"),subQ8,sQuery(id+"F0.wireOp",EDGE,"E27"),subQ7,subQ6,subQ5,subQ4,subQ3,subQ2,subQ1,subQ0])],"isStart":false})]})]});}
            var Q4;
            {var subQ0=sQuery(id+"F0.wireOp",EDGE,"E65");var subQ1=sQuery(id+"F0.wireOp",EDGE,"E64");var subQ2=sQuery(id+"F0.wireOp",EDGE,"E63.6");var subQ3=sQuery(id+"F0.wireOp",EDGE,"E63.5");var subQ4=sQuery(id+"F0.wireOp",EDGE,"E63.4");var subQ5=sQuery(id+"F0.wireOp",EDGE,"E63.2");var subQ6=sQuery(id+"F0.wireOp",EDGE,"E63.1");var subQ7=sQuery(id+"F0.wireOp",EDGE,"E63.0");var subQ8=sQuery(id+"F0.wireOp",EDGE,"E23");Q4=makeQuery(id+"F5.opChamfer","BLEND_EDGE",EDGE,{"disambiguationData":[OD(1.0)],"blendedFrom":[makeQuery(id+"F2.opExtrude","CAP_EDGE",EDGE,{"disambiguationData":[OSD([subQ8])],"isStart":false}),makeQuery(id+"F2.boolean.opBoolean","MERGE",FACE,{"derivedFrom":[makeQuery(id+"F1.opExtrude","CAP_FACE",FACE,{"disambiguationData":[OSD([sQuery(id+"F0.wireOp",EDGE,"E6"),sQuery(id+"F0.wireOp",EDGE,"E7"),sQuery(id+"F0.wireOp",EDGE,"E8"),sQuery(id+"F0.wireOp",EDGE,"E9"),sQuery(id+"F0.wireOp",EDGE,"E10"),sQuery(id+"F0.wireOp",EDGE,"E11"),sQuery(id+"F0.wireOp",EDGE,"E12"),sQuery(id+"F0.wireOp",EDGE,"E13"),sQuery(id+"F0.wireOp",EDGE,"E14"),sQuery(id+"F0.wireOp",EDGE,"E15"),sQuery(id+"F0.wireOp",EDGE,"E16"),sQuery(id+"F0.wireOp",EDGE,"E17"),sQuery(id+"F0.wireOp",EDGE,"E31"),sQuery(id+"F0.wireOp",EDGE,"E33"),sQuery(id+"F0.wireOp",EDGE,"E34"),sQuery(id+"F0.wireOp",EDGE,"E35"),sQuery(id+"F0.wireOp",EDGE,"E37"),sQuery(id+"F0.wireOp",EDGE,"E39"),sQuery(id+"F0.wireOp",EDGE,"E40"),sQuery(id+"F0.wireOp",EDGE,"E42"),sQuery(id+"F0.wireOp",EDGE,"E44"),sQuery(id+"F0.wireOp",EDGE,"E46"),sQuery(id+"F0.wireOp",EDGE,"E48"),sQuery(id+"F0.wireOp",EDGE,"E50"),sQuery(id+"F0.wireOp",EDGE,"E52"),sQuery(id+"F0.wireOp",EDGE,"E54"),sQuery(id+"F0.wireOp",EDGE,"E57"),sQuery(id+"F0.wireOp",EDGE,"E59"),sQuery(id+"F0.wireOp",EDGE,"E60"),sQuery(id+"F0.wireOp",EDGE,"E61"),sQuery(id+"F0.wireOp",EDGE,"E62"),subQ7,subQ6,subQ5,subQ4,subQ3,subQ2,subQ1,subQ0,sQuery(id+"F0.wireOp",EDGE,"E70"),sQuery(id+"F0.wireOp",EDGE,"E71"),sQuery(id+"F0.wireOp",EDGE,"E72"),sQuery(id+"F0.wireOp",EDGE,"E73.filletArc"),sQuery(id+"F0.wireOp",EDGE,"E74.filletArc"),sQuery(id+"F0.wireOp",EDGE,"E75.filletArc"),sQuery(id+"F0.wireOp",EDGE,"E76.filletArc"),sQuery(id+"F0.wireOp",EDGE,"E77.filletArc"),sQuery(id+"F0.wireOp",EDGE,"E78.filletArc"),sQuery(id+"F0.wireOp",EDGE,"E79.filletArc"),sQuery(id+"F0.wireOp",EDGE,"E80.filletArc"),sQuery(id+"F0.wireOp",EDGE,"E82.filletArc"),sQuery(id+"F0.wireOp",EDGE,"E83.filletArc")])],"isStart":false}),makeQuery(id+"F2.opExtrude","CAP_FACE",FACE,{"disambiguationData":[OSD([sQuery(id+"F0.wireOp",EDGE,"E19"),sQuery(id+"F0.wireOp",EDGE,"E20"),sQuery(id+"F0.wireOp",EDGE,"E22"),subQ8,sQuery(id+"F0.wireOp",EDGE,"E24"),sQuery(id+"F0.wireOp",EDGE,"E25"),sQuery(id+"F0.wireOp",EDGE,"E26"),sQuery(id+"F0.wireOp",EDGE,"E27"),subQ7,subQ6,subQ5,subQ4,subQ3,subQ2,subQ1,subQ0])],"isStart":false})]})],"blendedInto":[makeQuery(id+"F2.boolean.opBoolean","MERGE",FACE,{"derivedFrom":[makeQuery(id+"F1.opExtrude","CAP_FACE",FACE,{"disambiguationData":[OSD([sQuery(id+"F0.wireOp",EDGE,"E6"),sQuery(id+"F0.wireOp",EDGE,"E7"),sQuery(id+"F0.wireOp",EDGE,"E8"),sQuery(id+"F0.wireOp",EDGE,"E9"),sQuery(id+"F0.wireOp",EDGE,"E10"),sQuery(id+"F0.wireOp",EDGE,"E11"),sQuery(id+"F0.wireOp",EDGE,"E12"),sQuery(id+"F0.wireOp",EDGE,"E13"),sQuery(id+"F0.wireOp",EDGE,"E14"),sQuery(id+"F0.wireOp",EDGE,"E15"),sQuery(id+"F0.wireOp",EDGE,"E16"),sQuery(id+"F0.wireOp",EDGE,"E17"),sQuery(id+"F0.wireOp",EDGE,"E31"),sQuery(id+"F0.wireOp",EDGE,"E33"),sQuery(id+"F0.wireOp",EDGE,"E34"),sQuery(id+"F0.wireOp",EDGE,"E35"),sQuery(id+"F0.wireOp",EDGE,"E37"),sQuery(id+"F0.wireOp",EDGE,"E39"),sQuery(id+"F0.wireOp",EDGE,"E40"),sQuery(id+"F0.wireOp",EDGE,"E42"),sQuery(id+"F0.wireOp",EDGE,"E44"),sQuery(id+"F0.wireOp",EDGE,"E46"),sQuery(id+"F0.wireOp",EDGE,"E48"),sQuery(id+"F0.wireOp",EDGE,"E50"),sQuery(id+"F0.wireOp",EDGE,"E52"),sQuery(id+"F0.wireOp",EDGE,"E54"),sQuery(id+"F0.wireOp",EDGE,"E57"),sQuery(id+"F0.wireOp",EDGE,"E59"),sQuery(id+"F0.wireOp",EDGE,"E60"),sQuery(id+"F0.wireOp",EDGE,"E61"),sQuery(id+"F0.wireOp",EDGE,"E62"),subQ7,subQ6,subQ5,subQ4,subQ3,subQ2,subQ1,subQ0,sQuery(id+"F0.wireOp",EDGE,"E70"),sQuery(id+"F0.wireOp",EDGE,"E71"),sQuery(id+"F0.wireOp",EDGE,"E72"),sQuery(id+"F0.wireOp",EDGE,"E73.filletArc"),sQuery(id+"F0.wireOp",EDGE,"E74.filletArc"),sQuery(id+"F0.wireOp",EDGE,"E75.filletArc"),sQuery(id+"F0.wireOp",EDGE,"E76.filletArc"),sQuery(id+"F0.wireOp",EDGE,"E77.filletArc"),sQuery(id+"F0.wireOp",EDGE,"E78.filletArc"),sQuery(id+"F0.wireOp",EDGE,"E79.filletArc"),sQuery(id+"F0.wireOp",EDGE,"E80.filletArc"),sQuery(id+"F0.wireOp",EDGE,"E82.filletArc"),sQuery(id+"F0.wireOp",EDGE,"E83.filletArc")])],"isStart":false}),makeQuery(id+"F2.opExtrude","CAP_FACE",FACE,{"disambiguationData":[OSD([sQuery(id+"F0.wireOp",EDGE,"E19"),sQuery(id+"F0.wireOp",EDGE,"E20"),sQuery(id+"F0.wireOp",EDGE,"E22"),subQ8,sQuery(id+"F0.wireOp",EDGE,"E24"),sQuery(id+"F0.wireOp",EDGE,"E25"),sQuery(id+"F0.wireOp",EDGE,"E26"),sQuery(id+"F0.wireOp",EDGE,"E27"),subQ7,subQ6,subQ5,subQ4,subQ3,subQ2,subQ1,subQ0])],"isStart":false})]})]});}
            var Q5;
            {var subQ0=sQuery(id+"F0.wireOp",EDGE,"E65");var subQ1=sQuery(id+"F0.wireOp",EDGE,"E64");var subQ2=sQuery(id+"F0.wireOp",EDGE,"E63.6");var subQ3=sQuery(id+"F0.wireOp",EDGE,"E63.5");var subQ4=sQuery(id+"F0.wireOp",EDGE,"E63.4");var subQ5=sQuery(id+"F0.wireOp",EDGE,"E63.2");var subQ6=sQuery(id+"F0.wireOp",EDGE,"E63.1");var subQ7=sQuery(id+"F0.wireOp",EDGE,"E63.0");var subQ8=sQuery(id+"F0.wireOp",EDGE,"E23");Q5=makeQuery(id+"F5.opChamfer","BLEND_EDGE",EDGE,{"disambiguationData":[OD(0.0)],"blendedFrom":[makeQuery(id+"F2.opExtrude","CAP_EDGE",EDGE,{"disambiguationData":[OSD([subQ8])],"isStart":false}),makeQuery(id+"F2.boolean.opBoolean","MERGE",FACE,{"derivedFrom":[makeQuery(id+"F1.opExtrude","CAP_FACE",FACE,{"disambiguationData":[OSD([sQuery(id+"F0.wireOp",EDGE,"E6"),sQuery(id+"F0.wireOp",EDGE,"E7"),sQuery(id+"F0.wireOp",EDGE,"E8"),sQuery(id+"F0.wireOp",EDGE,"E9"),sQuery(id+"F0.wireOp",EDGE,"E10"),sQuery(id+"F0.wireOp",EDGE,"E11"),sQuery(id+"F0.wireOp",EDGE,"E12"),sQuery(id+"F0.wireOp",EDGE,"E13"),sQuery(id+"F0.wireOp",EDGE,"E14"),sQuery(id+"F0.wireOp",EDGE,"E15"),sQuery(id+"F0.wireOp",EDGE,"E16"),sQuery(id+"F0.wireOp",EDGE,"E17"),sQuery(id+"F0.wireOp",EDGE,"E31"),sQuery(id+"F0.wireOp",EDGE,"E33"),sQuery(id+"F0.wireOp",EDGE,"E34"),sQuery(id+"F0.wireOp",EDGE,"E35"),sQuery(id+"F0.wireOp",EDGE,"E37"),sQuery(id+"F0.wireOp",EDGE,"E39"),sQuery(id+"F0.wireOp",EDGE,"E40"),sQuery(id+"F0.wireOp",EDGE,"E42"),sQuery(id+"F0.wireOp",EDGE,"E44"),sQuery(id+"F0.wireOp",EDGE,"E46"),sQuery(id+"F0.wireOp",EDGE,"E48"),sQuery(id+"F0.wireOp",EDGE,"E50"),sQuery(id+"F0.wireOp",EDGE,"E52"),sQuery(id+"F0.wireOp",EDGE,"E54"),sQuery(id+"F0.wireOp",EDGE,"E57"),sQuery(id+"F0.wireOp",EDGE,"E59"),sQuery(id+"F0.wireOp",EDGE,"E60"),sQuery(id+"F0.wireOp",EDGE,"E61"),sQuery(id+"F0.wireOp",EDGE,"E62"),subQ7,subQ6,subQ5,subQ4,subQ3,subQ2,subQ1,subQ0,sQuery(id+"F0.wireOp",EDGE,"E70"),sQuery(id+"F0.wireOp",EDGE,"E71"),sQuery(id+"F0.wireOp",EDGE,"E72"),sQuery(id+"F0.wireOp",EDGE,"E73.filletArc"),sQuery(id+"F0.wireOp",EDGE,"E74.filletArc"),sQuery(id+"F0.wireOp",EDGE,"E75.filletArc"),sQuery(id+"F0.wireOp",EDGE,"E76.filletArc"),sQuery(id+"F0.wireOp",EDGE,"E77.filletArc"),sQuery(id+"F0.wireOp",EDGE,"E78.filletArc"),sQuery(id+"F0.wireOp",EDGE,"E79.filletArc"),sQuery(id+"F0.wireOp",EDGE,"E80.filletArc"),sQuery(id+"F0.wireOp",EDGE,"E82.filletArc"),sQuery(id+"F0.wireOp",EDGE,"E83.filletArc")])],"isStart":false}),makeQuery(id+"F2.opExtrude","CAP_FACE",FACE,{"disambiguationData":[OSD([sQuery(id+"F0.wireOp",EDGE,"E19"),sQuery(id+"F0.wireOp",EDGE,"E20"),sQuery(id+"F0.wireOp",EDGE,"E22"),subQ8,sQuery(id+"F0.wireOp",EDGE,"E24"),sQuery(id+"F0.wireOp",EDGE,"E25"),sQuery(id+"F0.wireOp",EDGE,"E26"),sQuery(id+"F0.wireOp",EDGE,"E27"),subQ7,subQ6,subQ5,subQ4,subQ3,subQ2,subQ1,subQ0])],"isStart":false})]})],"blendedInto":[makeQuery(id+"F2.boolean.opBoolean","MERGE",FACE,{"derivedFrom":[makeQuery(id+"F1.opExtrude","CAP_FACE",FACE,{"disambiguationData":[OSD([sQuery(id+"F0.wireOp",EDGE,"E6"),sQuery(id+"F0.wireOp",EDGE,"E7"),sQuery(id+"F0.wireOp",EDGE,"E8"),sQuery(id+"F0.wireOp",EDGE,"E9"),sQuery(id+"F0.wireOp",EDGE,"E10"),sQuery(id+"F0.wireOp",EDGE,"E11"),sQuery(id+"F0.wireOp",EDGE,"E12"),sQuery(id+"F0.wireOp",EDGE,"E13"),sQuery(id+"F0.wireOp",EDGE,"E14"),sQuery(id+"F0.wireOp",EDGE,"E15"),sQuery(id+"F0.wireOp",EDGE,"E16"),sQuery(id+"F0.wireOp",EDGE,"E17"),sQuery(id+"F0.wireOp",EDGE,"E31"),sQuery(id+"F0.wireOp",EDGE,"E33"),sQuery(id+"F0.wireOp",EDGE,"E34"),sQuery(id+"F0.wireOp",EDGE,"E35"),sQuery(id+"F0.wireOp",EDGE,"E37"),sQuery(id+"F0.wireOp",EDGE,"E39"),sQuery(id+"F0.wireOp",EDGE,"E40"),sQuery(id+"F0.wireOp",EDGE,"E42"),sQuery(id+"F0.wireOp",EDGE,"E44"),sQuery(id+"F0.wireOp",EDGE,"E46"),sQuery(id+"F0.wireOp",EDGE,"E48"),sQuery(id+"F0.wireOp",EDGE,"E50"),sQuery(id+"F0.wireOp",EDGE,"E52"),sQuery(id+"F0.wireOp",EDGE,"E54"),sQuery(id+"F0.wireOp",EDGE,"E57"),sQuery(id+"F0.wireOp",EDGE,"E59"),sQuery(id+"F0.wireOp",EDGE,"E60"),sQuery(id+"F0.wireOp",EDGE,"E61"),sQuery(id+"F0.wireOp",EDGE,"E62"),subQ7,subQ6,subQ5,subQ4,subQ3,subQ2,subQ1,subQ0,sQuery(id+"F0.wireOp",EDGE,"E70"),sQuery(id+"F0.wireOp",EDGE,"E71"),sQuery(id+"F0.wireOp",EDGE,"E72"),sQuery(id+"F0.wireOp",EDGE,"E73.filletArc"),sQuery(id+"F0.wireOp",EDGE,"E74.filletArc"),sQuery(id+"F0.wireOp",EDGE,"E75.filletArc"),sQuery(id+"F0.wireOp",EDGE,"E76.filletArc"),sQuery(id+"F0.wireOp",EDGE,"E77.filletArc"),sQuery(id+"F0.wireOp",EDGE,"E78.filletArc"),sQuery(id+"F0.wireOp",EDGE,"E79.filletArc"),sQuery(id+"F0.wireOp",EDGE,"E80.filletArc"),sQuery(id+"F0.wireOp",EDGE,"E82.filletArc"),sQuery(id+"F0.wireOp",EDGE,"E83.filletArc")])],"isStart":false}),makeQuery(id+"F2.opExtrude","CAP_FACE",FACE,{"disambiguationData":[OSD([sQuery(id+"F0.wireOp",EDGE,"E19"),sQuery(id+"F0.wireOp",EDGE,"E20"),sQuery(id+"F0.wireOp",EDGE,"E22"),subQ8,sQuery(id+"F0.wireOp",EDGE,"E24"),sQuery(id+"F0.wireOp",EDGE,"E25"),sQuery(id+"F0.wireOp",EDGE,"E26"),sQuery(id+"F0.wireOp",EDGE,"E27"),subQ7,subQ6,subQ5,subQ4,subQ3,subQ2,subQ1,subQ0])],"isStart":false})]})]});}
            var Q6;
            {var subQ0=sQuery(id+"F0.wireOp",EDGE,"E65");var subQ1=sQuery(id+"F0.wireOp",EDGE,"E64");var subQ2=sQuery(id+"F0.wireOp",EDGE,"E63.6");var subQ3=sQuery(id+"F0.wireOp",EDGE,"E63.5");var subQ4=sQuery(id+"F0.wireOp",EDGE,"E63.4");var subQ5=sQuery(id+"F0.wireOp",EDGE,"E63.2");var subQ6=sQuery(id+"F0.wireOp",EDGE,"E63.1");var subQ7=sQuery(id+"F0.wireOp",EDGE,"E63.0");var subQ8=sQuery(id+"F0.wireOp",EDGE,"E24");Q6=makeQuery(id+"F5.opChamfer","BLEND_EDGE",EDGE,{"disambiguationData":[OD(0.0)],"blendedFrom":[makeQuery(id+"F2.opExtrude","CAP_EDGE",EDGE,{"disambiguationData":[OSD([subQ8])],"isStart":true}),makeQuery(id+"F2.boolean.opBoolean","MERGE",FACE,{"derivedFrom":[makeQuery(id+"F1.opExtrude","CAP_FACE",FACE,{"disambiguationData":[OSD([sQuery(id+"F0.wireOp",EDGE,"E6"),sQuery(id+"F0.wireOp",EDGE,"E7"),sQuery(id+"F0.wireOp",EDGE,"E8"),sQuery(id+"F0.wireOp",EDGE,"E9"),sQuery(id+"F0.wireOp",EDGE,"E10"),sQuery(id+"F0.wireOp",EDGE,"E11"),sQuery(id+"F0.wireOp",EDGE,"E12"),sQuery(id+"F0.wireOp",EDGE,"E13"),sQuery(id+"F0.wireOp",EDGE,"E14"),sQuery(id+"F0.wireOp",EDGE,"E15"),sQuery(id+"F0.wireOp",EDGE,"E16"),sQuery(id+"F0.wireOp",EDGE,"E17"),sQuery(id+"F0.wireOp",EDGE,"E31"),sQuery(id+"F0.wireOp",EDGE,"E33"),sQuery(id+"F0.wireOp",EDGE,"E34"),sQuery(id+"F0.wireOp",EDGE,"E35"),sQuery(id+"F0.wireOp",EDGE,"E37"),sQuery(id+"F0.wireOp",EDGE,"E39"),sQuery(id+"F0.wireOp",EDGE,"E40"),sQuery(id+"F0.wireOp",EDGE,"E42"),sQuery(id+"F0.wireOp",EDGE,"E44"),sQuery(id+"F0.wireOp",EDGE,"E46"),sQuery(id+"F0.wireOp",EDGE,"E48"),sQuery(id+"F0.wireOp",EDGE,"E50"),sQuery(id+"F0.wireOp",EDGE,"E52"),sQuery(id+"F0.wireOp",EDGE,"E54"),sQuery(id+"F0.wireOp",EDGE,"E57"),sQuery(id+"F0.wireOp",EDGE,"E59"),sQuery(id+"F0.wireOp",EDGE,"E60"),sQuery(id+"F0.wireOp",EDGE,"E61"),sQuery(id+"F0.wireOp",EDGE,"E62"),subQ7,subQ6,subQ5,subQ4,subQ3,subQ2,subQ1,subQ0,sQuery(id+"F0.wireOp",EDGE,"E70"),sQuery(id+"F0.wireOp",EDGE,"E71"),sQuery(id+"F0.wireOp",EDGE,"E72"),sQuery(id+"F0.wireOp",EDGE,"E73.filletArc"),sQuery(id+"F0.wireOp",EDGE,"E74.filletArc"),sQuery(id+"F0.wireOp",EDGE,"E75.filletArc"),sQuery(id+"F0.wireOp",EDGE,"E76.filletArc"),sQuery(id+"F0.wireOp",EDGE,"E77.filletArc"),sQuery(id+"F0.wireOp",EDGE,"E78.filletArc"),sQuery(id+"F0.wireOp",EDGE,"E79.filletArc"),sQuery(id+"F0.wireOp",EDGE,"E80.filletArc"),sQuery(id+"F0.wireOp",EDGE,"E82.filletArc"),sQuery(id+"F0.wireOp",EDGE,"E83.filletArc")])],"isStart":true}),makeQuery(id+"F2.opExtrude","CAP_FACE",FACE,{"disambiguationData":[OSD([sQuery(id+"F0.wireOp",EDGE,"E19"),sQuery(id+"F0.wireOp",EDGE,"E20"),sQuery(id+"F0.wireOp",EDGE,"E22"),sQuery(id+"F0.wireOp",EDGE,"E23"),subQ8,sQuery(id+"F0.wireOp",EDGE,"E25"),sQuery(id+"F0.wireOp",EDGE,"E26"),sQuery(id+"F0.wireOp",EDGE,"E27"),subQ7,subQ6,subQ5,subQ4,subQ3,subQ2,subQ1,subQ0])],"isStart":true})]})],"blendedInto":[makeQuery(id+"F2.boolean.opBoolean","MERGE",FACE,{"derivedFrom":[makeQuery(id+"F1.opExtrude","CAP_FACE",FACE,{"disambiguationData":[OSD([sQuery(id+"F0.wireOp",EDGE,"E6"),sQuery(id+"F0.wireOp",EDGE,"E7"),sQuery(id+"F0.wireOp",EDGE,"E8"),sQuery(id+"F0.wireOp",EDGE,"E9"),sQuery(id+"F0.wireOp",EDGE,"E10"),sQuery(id+"F0.wireOp",EDGE,"E11"),sQuery(id+"F0.wireOp",EDGE,"E12"),sQuery(id+"F0.wireOp",EDGE,"E13"),sQuery(id+"F0.wireOp",EDGE,"E14"),sQuery(id+"F0.wireOp",EDGE,"E15"),sQuery(id+"F0.wireOp",EDGE,"E16"),sQuery(id+"F0.wireOp",EDGE,"E17"),sQuery(id+"F0.wireOp",EDGE,"E31"),sQuery(id+"F0.wireOp",EDGE,"E33"),sQuery(id+"F0.wireOp",EDGE,"E34"),sQuery(id+"F0.wireOp",EDGE,"E35"),sQuery(id+"F0.wireOp",EDGE,"E37"),sQuery(id+"F0.wireOp",EDGE,"E39"),sQuery(id+"F0.wireOp",EDGE,"E40"),sQuery(id+"F0.wireOp",EDGE,"E42"),sQuery(id+"F0.wireOp",EDGE,"E44"),sQuery(id+"F0.wireOp",EDGE,"E46"),sQuery(id+"F0.wireOp",EDGE,"E48"),sQuery(id+"F0.wireOp",EDGE,"E50"),sQuery(id+"F0.wireOp",EDGE,"E52"),sQuery(id+"F0.wireOp",EDGE,"E54"),sQuery(id+"F0.wireOp",EDGE,"E57"),sQuery(id+"F0.wireOp",EDGE,"E59"),sQuery(id+"F0.wireOp",EDGE,"E60"),sQuery(id+"F0.wireOp",EDGE,"E61"),sQuery(id+"F0.wireOp",EDGE,"E62"),subQ7,subQ6,subQ5,subQ4,subQ3,subQ2,subQ1,subQ0,sQuery(id+"F0.wireOp",EDGE,"E70"),sQuery(id+"F0.wireOp",EDGE,"E71"),sQuery(id+"F0.wireOp",EDGE,"E72"),sQuery(id+"F0.wireOp",EDGE,"E73.filletArc"),sQuery(id+"F0.wireOp",EDGE,"E74.filletArc"),sQuery(id+"F0.wireOp",EDGE,"E75.filletArc"),sQuery(id+"F0.wireOp",EDGE,"E76.filletArc"),sQuery(id+"F0.wireOp",EDGE,"E77.filletArc"),sQuery(id+"F0.wireOp",EDGE,"E78.filletArc"),sQuery(id+"F0.wireOp",EDGE,"E79.filletArc"),sQuery(id+"F0.wireOp",EDGE,"E80.filletArc"),sQuery(id+"F0.wireOp",EDGE,"E82.filletArc"),sQuery(id+"F0.wireOp",EDGE,"E83.filletArc")])],"isStart":true}),makeQuery(id+"F2.opExtrude","CAP_FACE",FACE,{"disambiguationData":[OSD([sQuery(id+"F0.wireOp",EDGE,"E19"),sQuery(id+"F0.wireOp",EDGE,"E20"),sQuery(id+"F0.wireOp",EDGE,"E22"),sQuery(id+"F0.wireOp",EDGE,"E23"),subQ8,sQuery(id+"F0.wireOp",EDGE,"E25"),sQuery(id+"F0.wireOp",EDGE,"E26"),sQuery(id+"F0.wireOp",EDGE,"E27"),subQ7,subQ6,subQ5,subQ4,subQ3,subQ2,subQ1,subQ0])],"isStart":true})]})]});}
            var Q7;
            {var subQ0=sQuery(id+"F0.wireOp",EDGE,"E65");var subQ1=sQuery(id+"F0.wireOp",EDGE,"E64");var subQ2=sQuery(id+"F0.wireOp",EDGE,"E63.6");var subQ3=sQuery(id+"F0.wireOp",EDGE,"E63.5");var subQ4=sQuery(id+"F0.wireOp",EDGE,"E63.4");var subQ5=sQuery(id+"F0.wireOp",EDGE,"E63.2");var subQ6=sQuery(id+"F0.wireOp",EDGE,"E63.1");var subQ7=sQuery(id+"F0.wireOp",EDGE,"E63.0");var subQ8=sQuery(id+"F0.wireOp",EDGE,"E23");Q7=makeQuery(id+"F5.opChamfer","BLEND_EDGE",EDGE,{"disambiguationData":[OD(1.0)],"blendedFrom":[makeQuery(id+"F2.opExtrude","CAP_EDGE",EDGE,{"disambiguationData":[OSD([subQ8])],"isStart":true}),makeQuery(id+"F2.boolean.opBoolean","MERGE",FACE,{"derivedFrom":[makeQuery(id+"F1.opExtrude","CAP_FACE",FACE,{"disambiguationData":[OSD([sQuery(id+"F0.wireOp",EDGE,"E6"),sQuery(id+"F0.wireOp",EDGE,"E7"),sQuery(id+"F0.wireOp",EDGE,"E8"),sQuery(id+"F0.wireOp",EDGE,"E9"),sQuery(id+"F0.wireOp",EDGE,"E10"),sQuery(id+"F0.wireOp",EDGE,"E11"),sQuery(id+"F0.wireOp",EDGE,"E12"),sQuery(id+"F0.wireOp",EDGE,"E13"),sQuery(id+"F0.wireOp",EDGE,"E14"),sQuery(id+"F0.wireOp",EDGE,"E15"),sQuery(id+"F0.wireOp",EDGE,"E16"),sQuery(id+"F0.wireOp",EDGE,"E17"),sQuery(id+"F0.wireOp",EDGE,"E31"),sQuery(id+"F0.wireOp",EDGE,"E33"),sQuery(id+"F0.wireOp",EDGE,"E34"),sQuery(id+"F0.wireOp",EDGE,"E35"),sQuery(id+"F0.wireOp",EDGE,"E37"),sQuery(id+"F0.wireOp",EDGE,"E39"),sQuery(id+"F0.wireOp",EDGE,"E40"),sQuery(id+"F0.wireOp",EDGE,"E42"),sQuery(id+"F0.wireOp",EDGE,"E44"),sQuery(id+"F0.wireOp",EDGE,"E46"),sQuery(id+"F0.wireOp",EDGE,"E48"),sQuery(id+"F0.wireOp",EDGE,"E50"),sQuery(id+"F0.wireOp",EDGE,"E52"),sQuery(id+"F0.wireOp",EDGE,"E54"),sQuery(id+"F0.wireOp",EDGE,"E57"),sQuery(id+"F0.wireOp",EDGE,"E59"),sQuery(id+"F0.wireOp",EDGE,"E60"),sQuery(id+"F0.wireOp",EDGE,"E61"),sQuery(id+"F0.wireOp",EDGE,"E62"),subQ7,subQ6,subQ5,subQ4,subQ3,subQ2,subQ1,subQ0,sQuery(id+"F0.wireOp",EDGE,"E70"),sQuery(id+"F0.wireOp",EDGE,"E71"),sQuery(id+"F0.wireOp",EDGE,"E72"),sQuery(id+"F0.wireOp",EDGE,"E73.filletArc"),sQuery(id+"F0.wireOp",EDGE,"E74.filletArc"),sQuery(id+"F0.wireOp",EDGE,"E75.filletArc"),sQuery(id+"F0.wireOp",EDGE,"E76.filletArc"),sQuery(id+"F0.wireOp",EDGE,"E77.filletArc"),sQuery(id+"F0.wireOp",EDGE,"E78.filletArc"),sQuery(id+"F0.wireOp",EDGE,"E79.filletArc"),sQuery(id+"F0.wireOp",EDGE,"E80.filletArc"),sQuery(id+"F0.wireOp",EDGE,"E82.filletArc"),sQuery(id+"F0.wireOp",EDGE,"E83.filletArc")])],"isStart":true}),makeQuery(id+"F2.opExtrude","CAP_FACE",FACE,{"disambiguationData":[OSD([sQuery(id+"F0.wireOp",EDGE,"E19"),sQuery(id+"F0.wireOp",EDGE,"E20"),sQuery(id+"F0.wireOp",EDGE,"E22"),subQ8,sQuery(id+"F0.wireOp",EDGE,"E24"),sQuery(id+"F0.wireOp",EDGE,"E25"),sQuery(id+"F0.wireOp",EDGE,"E26"),sQuery(id+"F0.wireOp",EDGE,"E27"),subQ7,subQ6,subQ5,subQ4,subQ3,subQ2,subQ1,subQ0])],"isStart":true})]})],"blendedInto":[makeQuery(id+"F2.boolean.opBoolean","MERGE",FACE,{"derivedFrom":[makeQuery(id+"F1.opExtrude","CAP_FACE",FACE,{"disambiguationData":[OSD([sQuery(id+"F0.wireOp",EDGE,"E6"),sQuery(id+"F0.wireOp",EDGE,"E7"),sQuery(id+"F0.wireOp",EDGE,"E8"),sQuery(id+"F0.wireOp",EDGE,"E9"),sQuery(id+"F0.wireOp",EDGE,"E10"),sQuery(id+"F0.wireOp",EDGE,"E11"),sQuery(id+"F0.wireOp",EDGE,"E12"),sQuery(id+"F0.wireOp",EDGE,"E13"),sQuery(id+"F0.wireOp",EDGE,"E14"),sQuery(id+"F0.wireOp",EDGE,"E15"),sQuery(id+"F0.wireOp",EDGE,"E16"),sQuery(id+"F0.wireOp",EDGE,"E17"),sQuery(id+"F0.wireOp",EDGE,"E31"),sQuery(id+"F0.wireOp",EDGE,"E33"),sQuery(id+"F0.wireOp",EDGE,"E34"),sQuery(id+"F0.wireOp",EDGE,"E35"),sQuery(id+"F0.wireOp",EDGE,"E37"),sQuery(id+"F0.wireOp",EDGE,"E39"),sQuery(id+"F0.wireOp",EDGE,"E40"),sQuery(id+"F0.wireOp",EDGE,"E42"),sQuery(id+"F0.wireOp",EDGE,"E44"),sQuery(id+"F0.wireOp",EDGE,"E46"),sQuery(id+"F0.wireOp",EDGE,"E48"),sQuery(id+"F0.wireOp",EDGE,"E50"),sQuery(id+"F0.wireOp",EDGE,"E52"),sQuery(id+"F0.wireOp",EDGE,"E54"),sQuery(id+"F0.wireOp",EDGE,"E57"),sQuery(id+"F0.wireOp",EDGE,"E59"),sQuery(id+"F0.wireOp",EDGE,"E60"),sQuery(id+"F0.wireOp",EDGE,"E61"),sQuery(id+"F0.wireOp",EDGE,"E62"),subQ7,subQ6,subQ5,subQ4,subQ3,subQ2,subQ1,subQ0,sQuery(id+"F0.wireOp",EDGE,"E70"),sQuery(id+"F0.wireOp",EDGE,"E71"),sQuery(id+"F0.wireOp",EDGE,"E72"),sQuery(id+"F0.wireOp",EDGE,"E73.filletArc"),sQuery(id+"F0.wireOp",EDGE,"E74.filletArc"),sQuery(id+"F0.wireOp",EDGE,"E75.filletArc"),sQuery(id+"F0.wireOp",EDGE,"E76.filletArc"),sQuery(id+"F0.wireOp",EDGE,"E77.filletArc"),sQuery(id+"F0.wireOp",EDGE,"E78.filletArc"),sQuery(id+"F0.wireOp",EDGE,"E79.filletArc"),sQuery(id+"F0.wireOp",EDGE,"E80.filletArc"),sQuery(id+"F0.wireOp",EDGE,"E82.filletArc"),sQuery(id+"F0.wireOp",EDGE,"E83.filletArc")])],"isStart":true}),makeQuery(id+"F2.opExtrude","CAP_FACE",FACE,{"disambiguationData":[OSD([sQuery(id+"F0.wireOp",EDGE,"E19"),sQuery(id+"F0.wireOp",EDGE,"E20"),sQuery(id+"F0.wireOp",EDGE,"E22"),subQ8,sQuery(id+"F0.wireOp",EDGE,"E24"),sQuery(id+"F0.wireOp",EDGE,"E25"),sQuery(id+"F0.wireOp",EDGE,"E26"),sQuery(id+"F0.wireOp",EDGE,"E27"),subQ7,subQ6,subQ5,subQ4,subQ3,subQ2,subQ1,subQ0])],"isStart":true})]})]});}
            var Q8;
            {var subQ0=sQuery(id+"F0.wireOp",EDGE,"E65");var subQ1=sQuery(id+"F0.wireOp",EDGE,"E64");var subQ2=sQuery(id+"F0.wireOp",EDGE,"E63.6");var subQ3=sQuery(id+"F0.wireOp",EDGE,"E63.5");var subQ4=sQuery(id+"F0.wireOp",EDGE,"E63.4");var subQ5=sQuery(id+"F0.wireOp",EDGE,"E63.2");var subQ6=sQuery(id+"F0.wireOp",EDGE,"E63.1");var subQ7=sQuery(id+"F0.wireOp",EDGE,"E63.0");var subQ8=sQuery(id+"F0.wireOp",EDGE,"E23");Q8=makeQuery(id+"F5.opChamfer","BLEND_EDGE",EDGE,{"disambiguationData":[OD(0.0)],"blendedFrom":[makeQuery(id+"F2.opExtrude","CAP_EDGE",EDGE,{"disambiguationData":[OSD([subQ8])],"isStart":true}),makeQuery(id+"F2.boolean.opBoolean","MERGE",FACE,{"derivedFrom":[makeQuery(id+"F1.opExtrude","CAP_FACE",FACE,{"disambiguationData":[OSD([sQuery(id+"F0.wireOp",EDGE,"E6"),sQuery(id+"F0.wireOp",EDGE,"E7"),sQuery(id+"F0.wireOp",EDGE,"E8"),sQuery(id+"F0.wireOp",EDGE,"E9"),sQuery(id+"F0.wireOp",EDGE,"E10"),sQuery(id+"F0.wireOp",EDGE,"E11"),sQuery(id+"F0.wireOp",EDGE,"E12"),sQuery(id+"F0.wireOp",EDGE,"E13"),sQuery(id+"F0.wireOp",EDGE,"E14"),sQuery(id+"F0.wireOp",EDGE,"E15"),sQuery(id+"F0.wireOp",EDGE,"E16"),sQuery(id+"F0.wireOp",EDGE,"E17"),sQuery(id+"F0.wireOp",EDGE,"E31"),sQuery(id+"F0.wireOp",EDGE,"E33"),sQuery(id+"F0.wireOp",EDGE,"E34"),sQuery(id+"F0.wireOp",EDGE,"E35"),sQuery(id+"F0.wireOp",EDGE,"E37"),sQuery(id+"F0.wireOp",EDGE,"E39"),sQuery(id+"F0.wireOp",EDGE,"E40"),sQuery(id+"F0.wireOp",EDGE,"E42"),sQuery(id+"F0.wireOp",EDGE,"E44"),sQuery(id+"F0.wireOp",EDGE,"E46"),sQuery(id+"F0.wireOp",EDGE,"E48"),sQuery(id+"F0.wireOp",EDGE,"E50"),sQuery(id+"F0.wireOp",EDGE,"E52"),sQuery(id+"F0.wireOp",EDGE,"E54"),sQuery(id+"F0.wireOp",EDGE,"E57"),sQuery(id+"F0.wireOp",EDGE,"E59"),sQuery(id+"F0.wireOp",EDGE,"E60"),sQuery(id+"F0.wireOp",EDGE,"E61"),sQuery(id+"F0.wireOp",EDGE,"E62"),subQ7,subQ6,subQ5,subQ4,subQ3,subQ2,subQ1,subQ0,sQuery(id+"F0.wireOp",EDGE,"E70"),sQuery(id+"F0.wireOp",EDGE,"E71"),sQuery(id+"F0.wireOp",EDGE,"E72"),sQuery(id+"F0.wireOp",EDGE,"E73.filletArc"),sQuery(id+"F0.wireOp",EDGE,"E74.filletArc"),sQuery(id+"F0.wireOp",EDGE,"E75.filletArc"),sQuery(id+"F0.wireOp",EDGE,"E76.filletArc"),sQuery(id+"F0.wireOp",EDGE,"E77.filletArc"),sQuery(id+"F0.wireOp",EDGE,"E78.filletArc"),sQuery(id+"F0.wireOp",EDGE,"E79.filletArc"),sQuery(id+"F0.wireOp",EDGE,"E80.filletArc"),sQuery(id+"F0.wireOp",EDGE,"E82.filletArc"),sQuery(id+"F0.wireOp",EDGE,"E83.filletArc")])],"isStart":true}),makeQuery(id+"F2.opExtrude","CAP_FACE",FACE,{"disambiguationData":[OSD([sQuery(id+"F0.wireOp",EDGE,"E19"),sQuery(id+"F0.wireOp",EDGE,"E20"),sQuery(id+"F0.wireOp",EDGE,"E22"),subQ8,sQuery(id+"F0.wireOp",EDGE,"E24"),sQuery(id+"F0.wireOp",EDGE,"E25"),sQuery(id+"F0.wireOp",EDGE,"E26"),sQuery(id+"F0.wireOp",EDGE,"E27"),subQ7,subQ6,subQ5,subQ4,subQ3,subQ2,subQ1,subQ0])],"isStart":true})]})],"blendedInto":[makeQuery(id+"F2.boolean.opBoolean","MERGE",FACE,{"derivedFrom":[makeQuery(id+"F1.opExtrude","CAP_FACE",FACE,{"disambiguationData":[OSD([sQuery(id+"F0.wireOp",EDGE,"E6"),sQuery(id+"F0.wireOp",EDGE,"E7"),sQuery(id+"F0.wireOp",EDGE,"E8"),sQuery(id+"F0.wireOp",EDGE,"E9"),sQuery(id+"F0.wireOp",EDGE,"E10"),sQuery(id+"F0.wireOp",EDGE,"E11"),sQuery(id+"F0.wireOp",EDGE,"E12"),sQuery(id+"F0.wireOp",EDGE,"E13"),sQuery(id+"F0.wireOp",EDGE,"E14"),sQuery(id+"F0.wireOp",EDGE,"E15"),sQuery(id+"F0.wireOp",EDGE,"E16"),sQuery(id+"F0.wireOp",EDGE,"E17"),sQuery(id+"F0.wireOp",EDGE,"E31"),sQuery(id+"F0.wireOp",EDGE,"E33"),sQuery(id+"F0.wireOp",EDGE,"E34"),sQuery(id+"F0.wireOp",EDGE,"E35"),sQuery(id+"F0.wireOp",EDGE,"E37"),sQuery(id+"F0.wireOp",EDGE,"E39"),sQuery(id+"F0.wireOp",EDGE,"E40"),sQuery(id+"F0.wireOp",EDGE,"E42"),sQuery(id+"F0.wireOp",EDGE,"E44"),sQuery(id+"F0.wireOp",EDGE,"E46"),sQuery(id+"F0.wireOp",EDGE,"E48"),sQuery(id+"F0.wireOp",EDGE,"E50"),sQuery(id+"F0.wireOp",EDGE,"E52"),sQuery(id+"F0.wireOp",EDGE,"E54"),sQuery(id+"F0.wireOp",EDGE,"E57"),sQuery(id+"F0.wireOp",EDGE,"E59"),sQuery(id+"F0.wireOp",EDGE,"E60"),sQuery(id+"F0.wireOp",EDGE,"E61"),sQuery(id+"F0.wireOp",EDGE,"E62"),subQ7,subQ6,subQ5,subQ4,subQ3,subQ2,subQ1,subQ0,sQuery(id+"F0.wireOp",EDGE,"E70"),sQuery(id+"F0.wireOp",EDGE,"E71"),sQuery(id+"F0.wireOp",EDGE,"E72"),sQuery(id+"F0.wireOp",EDGE,"E73.filletArc"),sQuery(id+"F0.wireOp",EDGE,"E74.filletArc"),sQuery(id+"F0.wireOp",EDGE,"E75.filletArc"),sQuery(id+"F0.wireOp",EDGE,"E76.filletArc"),sQuery(id+"F0.wireOp",EDGE,"E77.filletArc"),sQuery(id+"F0.wireOp",EDGE,"E78.filletArc"),sQuery(id+"F0.wireOp",EDGE,"E79.filletArc"),sQuery(id+"F0.wireOp",EDGE,"E80.filletArc"),sQuery(id+"F0.wireOp",EDGE,"E82.filletArc"),sQuery(id+"F0.wireOp",EDGE,"E83.filletArc")])],"isStart":true}),makeQuery(id+"F2.opExtrude","CAP_FACE",FACE,{"disambiguationData":[OSD([sQuery(id+"F0.wireOp",EDGE,"E19"),sQuery(id+"F0.wireOp",EDGE,"E20"),sQuery(id+"F0.wireOp",EDGE,"E22"),subQ8,sQuery(id+"F0.wireOp",EDGE,"E24"),sQuery(id+"F0.wireOp",EDGE,"E25"),sQuery(id+"F0.wireOp",EDGE,"E26"),sQuery(id+"F0.wireOp",EDGE,"E27"),subQ7,subQ6,subQ5,subQ4,subQ3,subQ2,subQ1,subQ0])],"isStart":true})]})]});}
            var Q9;
            {var subQ0=sQuery(id+"F0.wireOp",EDGE,"E65");var subQ1=sQuery(id+"F0.wireOp",EDGE,"E64");var subQ2=sQuery(id+"F0.wireOp",EDGE,"E63.6");var subQ3=sQuery(id+"F0.wireOp",EDGE,"E63.5");var subQ4=sQuery(id+"F0.wireOp",EDGE,"E63.4");var subQ5=sQuery(id+"F0.wireOp",EDGE,"E63.2");var subQ6=sQuery(id+"F0.wireOp",EDGE,"E63.1");var subQ7=sQuery(id+"F0.wireOp",EDGE,"E63.0");var subQ8=sQuery(id+"F0.wireOp",EDGE,"E26");Q9=makeQuery(id+"F4.opChamfer","BLEND_EDGE",EDGE,{"disambiguationData":[OD(1.0)],"blendedFrom":[makeQuery(id+"F2.opExtrude","CAP_EDGE",EDGE,{"disambiguationData":[OSD([subQ8])],"isStart":true}),makeQuery(id+"F2.boolean.opBoolean","MERGE",FACE,{"derivedFrom":[makeQuery(id+"F1.opExtrude","CAP_FACE",FACE,{"disambiguationData":[OSD([sQuery(id+"F0.wireOp",EDGE,"E6"),sQuery(id+"F0.wireOp",EDGE,"E7"),sQuery(id+"F0.wireOp",EDGE,"E8"),sQuery(id+"F0.wireOp",EDGE,"E9"),sQuery(id+"F0.wireOp",EDGE,"E10"),sQuery(id+"F0.wireOp",EDGE,"E11"),sQuery(id+"F0.wireOp",EDGE,"E12"),sQuery(id+"F0.wireOp",EDGE,"E13"),sQuery(id+"F0.wireOp",EDGE,"E14"),sQuery(id+"F0.wireOp",EDGE,"E15"),sQuery(id+"F0.wireOp",EDGE,"E16"),sQuery(id+"F0.wireOp",EDGE,"E17"),sQuery(id+"F0.wireOp",EDGE,"E31"),sQuery(id+"F0.wireOp",EDGE,"E33"),sQuery(id+"F0.wireOp",EDGE,"E34"),sQuery(id+"F0.wireOp",EDGE,"E35"),sQuery(id+"F0.wireOp",EDGE,"E37"),sQuery(id+"F0.wireOp",EDGE,"E39"),sQuery(id+"F0.wireOp",EDGE,"E40"),sQuery(id+"F0.wireOp",EDGE,"E42"),sQuery(id+"F0.wireOp",EDGE,"E44"),sQuery(id+"F0.wireOp",EDGE,"E46"),sQuery(id+"F0.wireOp",EDGE,"E48"),sQuery(id+"F0.wireOp",EDGE,"E50"),sQuery(id+"F0.wireOp",EDGE,"E52"),sQuery(id+"F0.wireOp",EDGE,"E54"),sQuery(id+"F0.wireOp",EDGE,"E57"),sQuery(id+"F0.wireOp",EDGE,"E59"),sQuery(id+"F0.wireOp",EDGE,"E60"),sQuery(id+"F0.wireOp",EDGE,"E61"),sQuery(id+"F0.wireOp",EDGE,"E62"),subQ7,subQ6,subQ5,subQ4,subQ3,subQ2,subQ1,subQ0,sQuery(id+"F0.wireOp",EDGE,"E70"),sQuery(id+"F0.wireOp",EDGE,"E71"),sQuery(id+"F0.wireOp",EDGE,"E72"),sQuery(id+"F0.wireOp",EDGE,"E73.filletArc"),sQuery(id+"F0.wireOp",EDGE,"E74.filletArc"),sQuery(id+"F0.wireOp",EDGE,"E75.filletArc"),sQuery(id+"F0.wireOp",EDGE,"E76.filletArc"),sQuery(id+"F0.wireOp",EDGE,"E77.filletArc"),sQuery(id+"F0.wireOp",EDGE,"E78.filletArc"),sQuery(id+"F0.wireOp",EDGE,"E79.filletArc"),sQuery(id+"F0.wireOp",EDGE,"E80.filletArc"),sQuery(id+"F0.wireOp",EDGE,"E82.filletArc"),sQuery(id+"F0.wireOp",EDGE,"E83.filletArc")])],"isStart":true}),makeQuery(id+"F2.opExtrude","CAP_FACE",FACE,{"disambiguationData":[OSD([sQuery(id+"F0.wireOp",EDGE,"E19"),sQuery(id+"F0.wireOp",EDGE,"E20"),sQuery(id+"F0.wireOp",EDGE,"E22"),sQuery(id+"F0.wireOp",EDGE,"E23"),sQuery(id+"F0.wireOp",EDGE,"E24"),sQuery(id+"F0.wireOp",EDGE,"E25"),subQ8,sQuery(id+"F0.wireOp",EDGE,"E27"),subQ7,subQ6,subQ5,subQ4,subQ3,subQ2,subQ1,subQ0])],"isStart":true})]})],"blendedInto":[makeQuery(id+"F2.boolean.opBoolean","MERGE",FACE,{"derivedFrom":[makeQuery(id+"F1.opExtrude","CAP_FACE",FACE,{"disambiguationData":[OSD([sQuery(id+"F0.wireOp",EDGE,"E6"),sQuery(id+"F0.wireOp",EDGE,"E7"),sQuery(id+"F0.wireOp",EDGE,"E8"),sQuery(id+"F0.wireOp",EDGE,"E9"),sQuery(id+"F0.wireOp",EDGE,"E10"),sQuery(id+"F0.wireOp",EDGE,"E11"),sQuery(id+"F0.wireOp",EDGE,"E12"),sQuery(id+"F0.wireOp",EDGE,"E13"),sQuery(id+"F0.wireOp",EDGE,"E14"),sQuery(id+"F0.wireOp",EDGE,"E15"),sQuery(id+"F0.wireOp",EDGE,"E16"),sQuery(id+"F0.wireOp",EDGE,"E17"),sQuery(id+"F0.wireOp",EDGE,"E31"),sQuery(id+"F0.wireOp",EDGE,"E33"),sQuery(id+"F0.wireOp",EDGE,"E34"),sQuery(id+"F0.wireOp",EDGE,"E35"),sQuery(id+"F0.wireOp",EDGE,"E37"),sQuery(id+"F0.wireOp",EDGE,"E39"),sQuery(id+"F0.wireOp",EDGE,"E40"),sQuery(id+"F0.wireOp",EDGE,"E42"),sQuery(id+"F0.wireOp",EDGE,"E44"),sQuery(id+"F0.wireOp",EDGE,"E46"),sQuery(id+"F0.wireOp",EDGE,"E48"),sQuery(id+"F0.wireOp",EDGE,"E50"),sQuery(id+"F0.wireOp",EDGE,"E52"),sQuery(id+"F0.wireOp",EDGE,"E54"),sQuery(id+"F0.wireOp",EDGE,"E57"),sQuery(id+"F0.wireOp",EDGE,"E59"),sQuery(id+"F0.wireOp",EDGE,"E60"),sQuery(id+"F0.wireOp",EDGE,"E61"),sQuery(id+"F0.wireOp",EDGE,"E62"),subQ7,subQ6,subQ5,subQ4,subQ3,subQ2,subQ1,subQ0,sQuery(id+"F0.wireOp",EDGE,"E70"),sQuery(id+"F0.wireOp",EDGE,"E71"),sQuery(id+"F0.wireOp",EDGE,"E72"),sQuery(id+"F0.wireOp",EDGE,"E73.filletArc"),sQuery(id+"F0.wireOp",EDGE,"E74.filletArc"),sQuery(id+"F0.wireOp",EDGE,"E75.filletArc"),sQuery(id+"F0.wireOp",EDGE,"E76.filletArc"),sQuery(id+"F0.wireOp",EDGE,"E77.filletArc"),sQuery(id+"F0.wireOp",EDGE,"E78.filletArc"),sQuery(id+"F0.wireOp",EDGE,"E79.filletArc"),sQuery(id+"F0.wireOp",EDGE,"E80.filletArc"),sQuery(id+"F0.wireOp",EDGE,"E82.filletArc"),sQuery(id+"F0.wireOp",EDGE,"E83.filletArc")])],"isStart":true}),makeQuery(id+"F2.opExtrude","CAP_FACE",FACE,{"disambiguationData":[OSD([sQuery(id+"F0.wireOp",EDGE,"E19"),sQuery(id+"F0.wireOp",EDGE,"E20"),sQuery(id+"F0.wireOp",EDGE,"E22"),sQuery(id+"F0.wireOp",EDGE,"E23"),sQuery(id+"F0.wireOp",EDGE,"E24"),sQuery(id+"F0.wireOp",EDGE,"E25"),subQ8,sQuery(id+"F0.wireOp",EDGE,"E27"),subQ7,subQ6,subQ5,subQ4,subQ3,subQ2,subQ1,subQ0])],"isStart":true})]})]});}
            var Q10;
            {var subQ0=sQuery(id+"F0.wireOp",EDGE,"E65");var subQ1=sQuery(id+"F0.wireOp",EDGE,"E64");var subQ2=sQuery(id+"F0.wireOp",EDGE,"E63.6");var subQ3=sQuery(id+"F0.wireOp",EDGE,"E63.5");var subQ4=sQuery(id+"F0.wireOp",EDGE,"E63.4");var subQ5=sQuery(id+"F0.wireOp",EDGE,"E63.2");var subQ6=sQuery(id+"F0.wireOp",EDGE,"E63.1");var subQ7=sQuery(id+"F0.wireOp",EDGE,"E63.0");var subQ8=sQuery(id+"F0.wireOp",EDGE,"E25");Q10=makeQuery(id+"F3.opChamfer","BLEND_EDGE",EDGE,{"blendedFrom":[makeQuery(id+"F2.opExtrude","CAP_EDGE",EDGE,{"disambiguationData":[OSD([subQ8])],"isStart":true}),makeQuery(id+"F2.boolean.opBoolean","MERGE",FACE,{"derivedFrom":[makeQuery(id+"F1.opExtrude","CAP_FACE",FACE,{"disambiguationData":[OSD([sQuery(id+"F0.wireOp",EDGE,"E6"),sQuery(id+"F0.wireOp",EDGE,"E7"),sQuery(id+"F0.wireOp",EDGE,"E8"),sQuery(id+"F0.wireOp",EDGE,"E9"),sQuery(id+"F0.wireOp",EDGE,"E10"),sQuery(id+"F0.wireOp",EDGE,"E11"),sQuery(id+"F0.wireOp",EDGE,"E12"),sQuery(id+"F0.wireOp",EDGE,"E13"),sQuery(id+"F0.wireOp",EDGE,"E14"),sQuery(id+"F0.wireOp",EDGE,"E15"),sQuery(id+"F0.wireOp",EDGE,"E16"),sQuery(id+"F0.wireOp",EDGE,"E17"),sQuery(id+"F0.wireOp",EDGE,"E31"),sQuery(id+"F0.wireOp",EDGE,"E33"),sQuery(id+"F0.wireOp",EDGE,"E34"),sQuery(id+"F0.wireOp",EDGE,"E35"),sQuery(id+"F0.wireOp",EDGE,"E37"),sQuery(id+"F0.wireOp",EDGE,"E39"),sQuery(id+"F0.wireOp",EDGE,"E40"),sQuery(id+"F0.wireOp",EDGE,"E42"),sQuery(id+"F0.wireOp",EDGE,"E44"),sQuery(id+"F0.wireOp",EDGE,"E46"),sQuery(id+"F0.wireOp",EDGE,"E48"),sQuery(id+"F0.wireOp",EDGE,"E50"),sQuery(id+"F0.wireOp",EDGE,"E52"),sQuery(id+"F0.wireOp",EDGE,"E54"),sQuery(id+"F0.wireOp",EDGE,"E57"),sQuery(id+"F0.wireOp",EDGE,"E59"),sQuery(id+"F0.wireOp",EDGE,"E60"),sQuery(id+"F0.wireOp",EDGE,"E61"),sQuery(id+"F0.wireOp",EDGE,"E62"),subQ7,subQ6,subQ5,subQ4,subQ3,subQ2,subQ1,subQ0,sQuery(id+"F0.wireOp",EDGE,"E70"),sQuery(id+"F0.wireOp",EDGE,"E71"),sQuery(id+"F0.wireOp",EDGE,"E72"),sQuery(id+"F0.wireOp",EDGE,"E73.filletArc"),sQuery(id+"F0.wireOp",EDGE,"E74.filletArc"),sQuery(id+"F0.wireOp",EDGE,"E75.filletArc"),sQuery(id+"F0.wireOp",EDGE,"E76.filletArc"),sQuery(id+"F0.wireOp",EDGE,"E77.filletArc"),sQuery(id+"F0.wireOp",EDGE,"E78.filletArc"),sQuery(id+"F0.wireOp",EDGE,"E79.filletArc"),sQuery(id+"F0.wireOp",EDGE,"E80.filletArc"),sQuery(id+"F0.wireOp",EDGE,"E82.filletArc"),sQuery(id+"F0.wireOp",EDGE,"E83.filletArc")])],"isStart":true}),makeQuery(id+"F2.opExtrude","CAP_FACE",FACE,{"disambiguationData":[OSD([sQuery(id+"F0.wireOp",EDGE,"E19"),sQuery(id+"F0.wireOp",EDGE,"E20"),sQuery(id+"F0.wireOp",EDGE,"E22"),sQuery(id+"F0.wireOp",EDGE,"E23"),sQuery(id+"F0.wireOp",EDGE,"E24"),subQ8,sQuery(id+"F0.wireOp",EDGE,"E26"),sQuery(id+"F0.wireOp",EDGE,"E27"),subQ7,subQ6,subQ5,subQ4,subQ3,subQ2,subQ1,subQ0])],"isStart":true})]})],"blendedInto":[makeQuery(id+"F2.boolean.opBoolean","MERGE",FACE,{"derivedFrom":[makeQuery(id+"F1.opExtrude","CAP_FACE",FACE,{"disambiguationData":[OSD([sQuery(id+"F0.wireOp",EDGE,"E6"),sQuery(id+"F0.wireOp",EDGE,"E7"),sQuery(id+"F0.wireOp",EDGE,"E8"),sQuery(id+"F0.wireOp",EDGE,"E9"),sQuery(id+"F0.wireOp",EDGE,"E10"),sQuery(id+"F0.wireOp",EDGE,"E11"),sQuery(id+"F0.wireOp",EDGE,"E12"),sQuery(id+"F0.wireOp",EDGE,"E13"),sQuery(id+"F0.wireOp",EDGE,"E14"),sQuery(id+"F0.wireOp",EDGE,"E15"),sQuery(id+"F0.wireOp",EDGE,"E16"),sQuery(id+"F0.wireOp",EDGE,"E17"),sQuery(id+"F0.wireOp",EDGE,"E31"),sQuery(id+"F0.wireOp",EDGE,"E33"),sQuery(id+"F0.wireOp",EDGE,"E34"),sQuery(id+"F0.wireOp",EDGE,"E35"),sQuery(id+"F0.wireOp",EDGE,"E37"),sQuery(id+"F0.wireOp",EDGE,"E39"),sQuery(id+"F0.wireOp",EDGE,"E40"),sQuery(id+"F0.wireOp",EDGE,"E42"),sQuery(id+"F0.wireOp",EDGE,"E44"),sQuery(id+"F0.wireOp",EDGE,"E46"),sQuery(id+"F0.wireOp",EDGE,"E48"),sQuery(id+"F0.wireOp",EDGE,"E50"),sQuery(id+"F0.wireOp",EDGE,"E52"),sQuery(id+"F0.wireOp",EDGE,"E54"),sQuery(id+"F0.wireOp",EDGE,"E57"),sQuery(id+"F0.wireOp",EDGE,"E59"),sQuery(id+"F0.wireOp",EDGE,"E60"),sQuery(id+"F0.wireOp",EDGE,"E61"),sQuery(id+"F0.wireOp",EDGE,"E62"),subQ7,subQ6,subQ5,subQ4,subQ3,subQ2,subQ1,subQ0,sQuery(id+"F0.wireOp",EDGE,"E70"),sQuery(id+"F0.wireOp",EDGE,"E71"),sQuery(id+"F0.wireOp",EDGE,"E72"),sQuery(id+"F0.wireOp",EDGE,"E73.filletArc"),sQuery(id+"F0.wireOp",EDGE,"E74.filletArc"),sQuery(id+"F0.wireOp",EDGE,"E75.filletArc"),sQuery(id+"F0.wireOp",EDGE,"E76.filletArc"),sQuery(id+"F0.wireOp",EDGE,"E77.filletArc"),sQuery(id+"F0.wireOp",EDGE,"E78.filletArc"),sQuery(id+"F0.wireOp",EDGE,"E79.filletArc"),sQuery(id+"F0.wireOp",EDGE,"E80.filletArc"),sQuery(id+"F0.wireOp",EDGE,"E82.filletArc"),sQuery(id+"F0.wireOp",EDGE,"E83.filletArc")])],"isStart":true}),makeQuery(id+"F2.opExtrude","CAP_FACE",FACE,{"disambiguationData":[OSD([sQuery(id+"F0.wireOp",EDGE,"E19"),sQuery(id+"F0.wireOp",EDGE,"E20"),sQuery(id+"F0.wireOp",EDGE,"E22"),sQuery(id+"F0.wireOp",EDGE,"E23"),sQuery(id+"F0.wireOp",EDGE,"E24"),subQ8,sQuery(id+"F0.wireOp",EDGE,"E26"),sQuery(id+"F0.wireOp",EDGE,"E27"),subQ7,subQ6,subQ5,subQ4,subQ3,subQ2,subQ1,subQ0])],"isStart":true})]})]});}
            var Q11;
            {var subQ0=sQuery(id+"F0.wireOp",EDGE,"E65");var subQ1=sQuery(id+"F0.wireOp",EDGE,"E64");var subQ2=sQuery(id+"F0.wireOp",EDGE,"E63.6");var subQ3=sQuery(id+"F0.wireOp",EDGE,"E63.5");var subQ4=sQuery(id+"F0.wireOp",EDGE,"E63.4");var subQ5=sQuery(id+"F0.wireOp",EDGE,"E63.2");var subQ6=sQuery(id+"F0.wireOp",EDGE,"E63.1");var subQ7=sQuery(id+"F0.wireOp",EDGE,"E63.0");var subQ8=sQuery(id+"F0.wireOp",EDGE,"E27");Q11=makeQuery(id+"F4.opChamfer","BLEND_EDGE",EDGE,{"blendedFrom":[makeQuery(id+"F2.opExtrude","CAP_EDGE",EDGE,{"disambiguationData":[OSD([subQ8])],"isStart":true}),makeQuery(id+"F2.boolean.opBoolean","MERGE",FACE,{"derivedFrom":[makeQuery(id+"F1.opExtrude","CAP_FACE",FACE,{"disambiguationData":[OSD([sQuery(id+"F0.wireOp",EDGE,"E6"),sQuery(id+"F0.wireOp",EDGE,"E7"),sQuery(id+"F0.wireOp",EDGE,"E8"),sQuery(id+"F0.wireOp",EDGE,"E9"),sQuery(id+"F0.wireOp",EDGE,"E10"),sQuery(id+"F0.wireOp",EDGE,"E11"),sQuery(id+"F0.wireOp",EDGE,"E12"),sQuery(id+"F0.wireOp",EDGE,"E13"),sQuery(id+"F0.wireOp",EDGE,"E14"),sQuery(id+"F0.wireOp",EDGE,"E15"),sQuery(id+"F0.wireOp",EDGE,"E16"),sQuery(id+"F0.wireOp",EDGE,"E17"),sQuery(id+"F0.wireOp",EDGE,"E31"),sQuery(id+"F0.wireOp",EDGE,"E33"),sQuery(id+"F0.wireOp",EDGE,"E34"),sQuery(id+"F0.wireOp",EDGE,"E35"),sQuery(id+"F0.wireOp",EDGE,"E37"),sQuery(id+"F0.wireOp",EDGE,"E39"),sQuery(id+"F0.wireOp",EDGE,"E40"),sQuery(id+"F0.wireOp",EDGE,"E42"),sQuery(id+"F0.wireOp",EDGE,"E44"),sQuery(id+"F0.wireOp",EDGE,"E46"),sQuery(id+"F0.wireOp",EDGE,"E48"),sQuery(id+"F0.wireOp",EDGE,"E50"),sQuery(id+"F0.wireOp",EDGE,"E52"),sQuery(id+"F0.wireOp",EDGE,"E54"),sQuery(id+"F0.wireOp",EDGE,"E57"),sQuery(id+"F0.wireOp",EDGE,"E59"),sQuery(id+"F0.wireOp",EDGE,"E60"),sQuery(id+"F0.wireOp",EDGE,"E61"),sQuery(id+"F0.wireOp",EDGE,"E62"),subQ7,subQ6,subQ5,subQ4,subQ3,subQ2,subQ1,subQ0,sQuery(id+"F0.wireOp",EDGE,"E70"),sQuery(id+"F0.wireOp",EDGE,"E71"),sQuery(id+"F0.wireOp",EDGE,"E72"),sQuery(id+"F0.wireOp",EDGE,"E73.filletArc"),sQuery(id+"F0.wireOp",EDGE,"E74.filletArc"),sQuery(id+"F0.wireOp",EDGE,"E75.filletArc"),sQuery(id+"F0.wireOp",EDGE,"E76.filletArc"),sQuery(id+"F0.wireOp",EDGE,"E77.filletArc"),sQuery(id+"F0.wireOp",EDGE,"E78.filletArc"),sQuery(id+"F0.wireOp",EDGE,"E79.filletArc"),sQuery(id+"F0.wireOp",EDGE,"E80.filletArc"),sQuery(id+"F0.wireOp",EDGE,"E82.filletArc"),sQuery(id+"F0.wireOp",EDGE,"E83.filletArc")])],"isStart":true}),makeQuery(id+"F2.opExtrude","CAP_FACE",FACE,{"disambiguationData":[OSD([sQuery(id+"F0.wireOp",EDGE,"E19"),sQuery(id+"F0.wireOp",EDGE,"E20"),sQuery(id+"F0.wireOp",EDGE,"E22"),sQuery(id+"F0.wireOp",EDGE,"E23"),sQuery(id+"F0.wireOp",EDGE,"E24"),sQuery(id+"F0.wireOp",EDGE,"E25"),sQuery(id+"F0.wireOp",EDGE,"E26"),subQ8,subQ7,subQ6,subQ5,subQ4,subQ3,subQ2,subQ1,subQ0])],"isStart":true})]})],"blendedInto":[makeQuery(id+"F2.boolean.opBoolean","MERGE",FACE,{"derivedFrom":[makeQuery(id+"F1.opExtrude","CAP_FACE",FACE,{"disambiguationData":[OSD([sQuery(id+"F0.wireOp",EDGE,"E6"),sQuery(id+"F0.wireOp",EDGE,"E7"),sQuery(id+"F0.wireOp",EDGE,"E8"),sQuery(id+"F0.wireOp",EDGE,"E9"),sQuery(id+"F0.wireOp",EDGE,"E10"),sQuery(id+"F0.wireOp",EDGE,"E11"),sQuery(id+"F0.wireOp",EDGE,"E12"),sQuery(id+"F0.wireOp",EDGE,"E13"),sQuery(id+"F0.wireOp",EDGE,"E14"),sQuery(id+"F0.wireOp",EDGE,"E15"),sQuery(id+"F0.wireOp",EDGE,"E16"),sQuery(id+"F0.wireOp",EDGE,"E17"),sQuery(id+"F0.wireOp",EDGE,"E31"),sQuery(id+"F0.wireOp",EDGE,"E33"),sQuery(id+"F0.wireOp",EDGE,"E34"),sQuery(id+"F0.wireOp",EDGE,"E35"),sQuery(id+"F0.wireOp",EDGE,"E37"),sQuery(id+"F0.wireOp",EDGE,"E39"),sQuery(id+"F0.wireOp",EDGE,"E40"),sQuery(id+"F0.wireOp",EDGE,"E42"),sQuery(id+"F0.wireOp",EDGE,"E44"),sQuery(id+"F0.wireOp",EDGE,"E46"),sQuery(id+"F0.wireOp",EDGE,"E48"),sQuery(id+"F0.wireOp",EDGE,"E50"),sQuery(id+"F0.wireOp",EDGE,"E52"),sQuery(id+"F0.wireOp",EDGE,"E54"),sQuery(id+"F0.wireOp",EDGE,"E57"),sQuery(id+"F0.wireOp",EDGE,"E59"),sQuery(id+"F0.wireOp",EDGE,"E60"),sQuery(id+"F0.wireOp",EDGE,"E61"),sQuery(id+"F0.wireOp",EDGE,"E62"),subQ7,subQ6,subQ5,subQ4,subQ3,subQ2,subQ1,subQ0,sQuery(id+"F0.wireOp",EDGE,"E70"),sQuery(id+"F0.wireOp",EDGE,"E71"),sQuery(id+"F0.wireOp",EDGE,"E72"),sQuery(id+"F0.wireOp",EDGE,"E73.filletArc"),sQuery(id+"F0.wireOp",EDGE,"E74.filletArc"),sQuery(id+"F0.wireOp",EDGE,"E75.filletArc"),sQuery(id+"F0.wireOp",EDGE,"E76.filletArc"),sQuery(id+"F0.wireOp",EDGE,"E77.filletArc"),sQuery(id+"F0.wireOp",EDGE,"E78.filletArc"),sQuery(id+"F0.wireOp",EDGE,"E79.filletArc"),sQuery(id+"F0.wireOp",EDGE,"E80.filletArc"),sQuery(id+"F0.wireOp",EDGE,"E82.filletArc"),sQuery(id+"F0.wireOp",EDGE,"E83.filletArc")])],"isStart":true}),makeQuery(id+"F2.opExtrude","CAP_FACE",FACE,{"disambiguationData":[OSD([sQuery(id+"F0.wireOp",EDGE,"E19"),sQuery(id+"F0.wireOp",EDGE,"E20"),sQuery(id+"F0.wireOp",EDGE,"E22"),sQuery(id+"F0.wireOp",EDGE,"E23"),sQuery(id+"F0.wireOp",EDGE,"E24"),sQuery(id+"F0.wireOp",EDGE,"E25"),sQuery(id+"F0.wireOp",EDGE,"E26"),subQ8,subQ7,subQ6,subQ5,subQ4,subQ3,subQ2,subQ1,subQ0])],"isStart":true})]})]});}
            var Q12;
            {var subQ0=sQuery(id+"F0.wireOp",EDGE,"E65");var subQ1=sQuery(id+"F0.wireOp",EDGE,"E64");var subQ2=sQuery(id+"F0.wireOp",EDGE,"E63.6");var subQ3=sQuery(id+"F0.wireOp",EDGE,"E63.5");var subQ4=sQuery(id+"F0.wireOp",EDGE,"E63.4");var subQ5=sQuery(id+"F0.wireOp",EDGE,"E63.2");var subQ6=sQuery(id+"F0.wireOp",EDGE,"E63.1");var subQ7=sQuery(id+"F0.wireOp",EDGE,"E63.0");var subQ8=sQuery(id+"F0.wireOp",EDGE,"E27");Q12=makeQuery(id+"F4.opChamfer","BLEND_EDGE",EDGE,{"blendedFrom":[makeQuery(id+"F2.opExtrude","CAP_EDGE",EDGE,{"disambiguationData":[OSD([subQ8])],"isStart":false}),makeQuery(id+"F2.boolean.opBoolean","MERGE",FACE,{"derivedFrom":[makeQuery(id+"F1.opExtrude","CAP_FACE",FACE,{"disambiguationData":[OSD([sQuery(id+"F0.wireOp",EDGE,"E6"),sQuery(id+"F0.wireOp",EDGE,"E7"),sQuery(id+"F0.wireOp",EDGE,"E8"),sQuery(id+"F0.wireOp",EDGE,"E9"),sQuery(id+"F0.wireOp",EDGE,"E10"),sQuery(id+"F0.wireOp",EDGE,"E11"),sQuery(id+"F0.wireOp",EDGE,"E12"),sQuery(id+"F0.wireOp",EDGE,"E13"),sQuery(id+"F0.wireOp",EDGE,"E14"),sQuery(id+"F0.wireOp",EDGE,"E15"),sQuery(id+"F0.wireOp",EDGE,"E16"),sQuery(id+"F0.wireOp",EDGE,"E17"),sQuery(id+"F0.wireOp",EDGE,"E31"),sQuery(id+"F0.wireOp",EDGE,"E33"),sQuery(id+"F0.wireOp",EDGE,"E34"),sQuery(id+"F0.wireOp",EDGE,"E35"),sQuery(id+"F0.wireOp",EDGE,"E37"),sQuery(id+"F0.wireOp",EDGE,"E39"),sQuery(id+"F0.wireOp",EDGE,"E40"),sQuery(id+"F0.wireOp",EDGE,"E42"),sQuery(id+"F0.wireOp",EDGE,"E44"),sQuery(id+"F0.wireOp",EDGE,"E46"),sQuery(id+"F0.wireOp",EDGE,"E48"),sQuery(id+"F0.wireOp",EDGE,"E50"),sQuery(id+"F0.wireOp",EDGE,"E52"),sQuery(id+"F0.wireOp",EDGE,"E54"),sQuery(id+"F0.wireOp",EDGE,"E57"),sQuery(id+"F0.wireOp",EDGE,"E59"),sQuery(id+"F0.wireOp",EDGE,"E60"),sQuery(id+"F0.wireOp",EDGE,"E61"),sQuery(id+"F0.wireOp",EDGE,"E62"),subQ7,subQ6,subQ5,subQ4,subQ3,subQ2,subQ1,subQ0,sQuery(id+"F0.wireOp",EDGE,"E70"),sQuery(id+"F0.wireOp",EDGE,"E71"),sQuery(id+"F0.wireOp",EDGE,"E72"),sQuery(id+"F0.wireOp",EDGE,"E73.filletArc"),sQuery(id+"F0.wireOp",EDGE,"E74.filletArc"),sQuery(id+"F0.wireOp",EDGE,"E75.filletArc"),sQuery(id+"F0.wireOp",EDGE,"E76.filletArc"),sQuery(id+"F0.wireOp",EDGE,"E77.filletArc"),sQuery(id+"F0.wireOp",EDGE,"E78.filletArc"),sQuery(id+"F0.wireOp",EDGE,"E79.filletArc"),sQuery(id+"F0.wireOp",EDGE,"E80.filletArc"),sQuery(id+"F0.wireOp",EDGE,"E82.filletArc"),sQuery(id+"F0.wireOp",EDGE,"E83.filletArc")])],"isStart":false}),makeQuery(id+"F2.opExtrude","CAP_FACE",FACE,{"disambiguationData":[OSD([sQuery(id+"F0.wireOp",EDGE,"E19"),sQuery(id+"F0.wireOp",EDGE,"E20"),sQuery(id+"F0.wireOp",EDGE,"E22"),sQuery(id+"F0.wireOp",EDGE,"E23"),sQuery(id+"F0.wireOp",EDGE,"E24"),sQuery(id+"F0.wireOp",EDGE,"E25"),sQuery(id+"F0.wireOp",EDGE,"E26"),subQ8,subQ7,subQ6,subQ5,subQ4,subQ3,subQ2,subQ1,subQ0])],"isStart":false})]})],"blendedInto":[makeQuery(id+"F2.boolean.opBoolean","MERGE",FACE,{"derivedFrom":[makeQuery(id+"F1.opExtrude","CAP_FACE",FACE,{"disambiguationData":[OSD([sQuery(id+"F0.wireOp",EDGE,"E6"),sQuery(id+"F0.wireOp",EDGE,"E7"),sQuery(id+"F0.wireOp",EDGE,"E8"),sQuery(id+"F0.wireOp",EDGE,"E9"),sQuery(id+"F0.wireOp",EDGE,"E10"),sQuery(id+"F0.wireOp",EDGE,"E11"),sQuery(id+"F0.wireOp",EDGE,"E12"),sQuery(id+"F0.wireOp",EDGE,"E13"),sQuery(id+"F0.wireOp",EDGE,"E14"),sQuery(id+"F0.wireOp",EDGE,"E15"),sQuery(id+"F0.wireOp",EDGE,"E16"),sQuery(id+"F0.wireOp",EDGE,"E17"),sQuery(id+"F0.wireOp",EDGE,"E31"),sQuery(id+"F0.wireOp",EDGE,"E33"),sQuery(id+"F0.wireOp",EDGE,"E34"),sQuery(id+"F0.wireOp",EDGE,"E35"),sQuery(id+"F0.wireOp",EDGE,"E37"),sQuery(id+"F0.wireOp",EDGE,"E39"),sQuery(id+"F0.wireOp",EDGE,"E40"),sQuery(id+"F0.wireOp",EDGE,"E42"),sQuery(id+"F0.wireOp",EDGE,"E44"),sQuery(id+"F0.wireOp",EDGE,"E46"),sQuery(id+"F0.wireOp",EDGE,"E48"),sQuery(id+"F0.wireOp",EDGE,"E50"),sQuery(id+"F0.wireOp",EDGE,"E52"),sQuery(id+"F0.wireOp",EDGE,"E54"),sQuery(id+"F0.wireOp",EDGE,"E57"),sQuery(id+"F0.wireOp",EDGE,"E59"),sQuery(id+"F0.wireOp",EDGE,"E60"),sQuery(id+"F0.wireOp",EDGE,"E61"),sQuery(id+"F0.wireOp",EDGE,"E62"),subQ7,subQ6,subQ5,subQ4,subQ3,subQ2,subQ1,subQ0,sQuery(id+"F0.wireOp",EDGE,"E70"),sQuery(id+"F0.wireOp",EDGE,"E71"),sQuery(id+"F0.wireOp",EDGE,"E72"),sQuery(id+"F0.wireOp",EDGE,"E73.filletArc"),sQuery(id+"F0.wireOp",EDGE,"E74.filletArc"),sQuery(id+"F0.wireOp",EDGE,"E75.filletArc"),sQuery(id+"F0.wireOp",EDGE,"E76.filletArc"),sQuery(id+"F0.wireOp",EDGE,"E77.filletArc"),sQuery(id+"F0.wireOp",EDGE,"E78.filletArc"),sQuery(id+"F0.wireOp",EDGE,"E79.filletArc"),sQuery(id+"F0.wireOp",EDGE,"E80.filletArc"),sQuery(id+"F0.wireOp",EDGE,"E82.filletArc"),sQuery(id+"F0.wireOp",EDGE,"E83.filletArc")])],"isStart":false}),makeQuery(id+"F2.opExtrude","CAP_FACE",FACE,{"disambiguationData":[OSD([sQuery(id+"F0.wireOp",EDGE,"E19"),sQuery(id+"F0.wireOp",EDGE,"E20"),sQuery(id+"F0.wireOp",EDGE,"E22"),sQuery(id+"F0.wireOp",EDGE,"E23"),sQuery(id+"F0.wireOp",EDGE,"E24"),sQuery(id+"F0.wireOp",EDGE,"E25"),sQuery(id+"F0.wireOp",EDGE,"E26"),subQ8,subQ7,subQ6,subQ5,subQ4,subQ3,subQ2,subQ1,subQ0])],"isStart":false})]})]});}
            fillet(context, id + "F10", {"entities" : qUnion([Q0, Q1, Q2, Q3, Q4, Q5, Q6, Q7, Q8, Q9, Q10, Q11, Q12]), "radius" : 5.08 * mm, "tangentPropagation" : true, "allowEdgeOverflow" : false});
        }
    });
